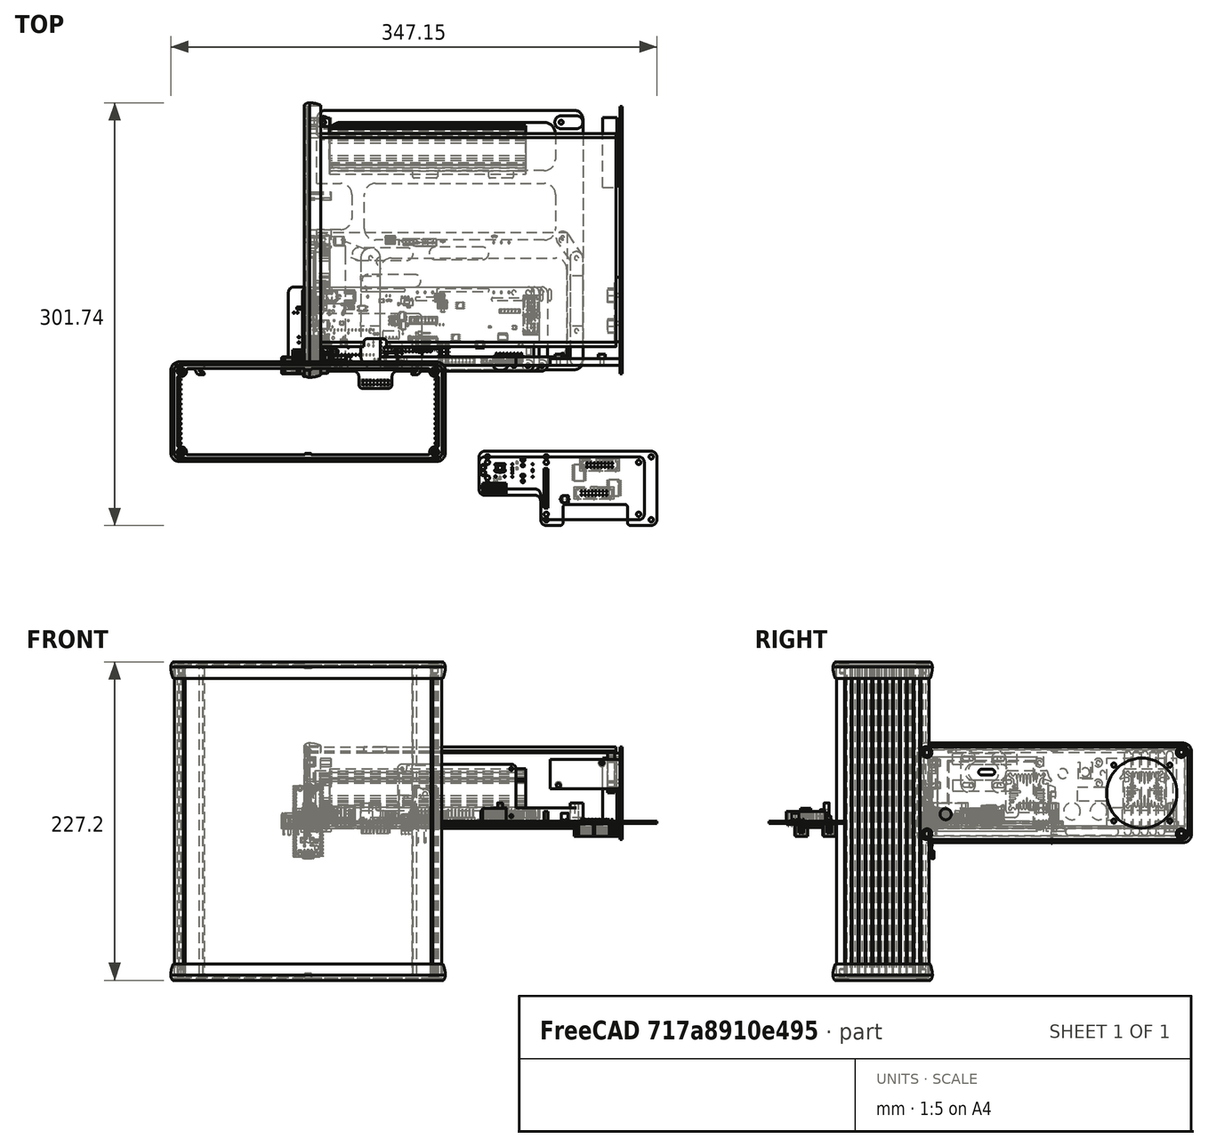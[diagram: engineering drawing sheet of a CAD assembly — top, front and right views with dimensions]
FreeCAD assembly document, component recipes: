
FREECAD ASSEMBLY — COMPONENT RECIPES ("EL-Load-CaseV4")

This assembly document has 17 components, labeled P0..P16 below (a component is one placed body or linked part). 7 of them carry a construction recipe — the FreeCAD feature program that regenerates the part from scratch, quoted from this document or its linked companion documents; the rest are supplied as boundary geometry only. No exploded tour is included for this assembly.
COMPONENT P0 — geometry summary ("EL-Load-Analog"; no construction recipe available for this part):
  bounding box: 188.2 x 95.0 x 51.8 mm
  tessellated surface: 174,292 triangles
  volume: 45099 mm^3 (5% of its bounding box)
COMPONENT P1 — geometry summary ("EL-Load-Analog001"; no construction recipe available for this part):
  bounding box: 185.0 x 95.0 x 41.1 mm
  tessellated surface: 106,424 triangles
  volume: 35915 mm^3 (5% of its bounding box)
COMPONENT P2 — geometry summary ("EL-Load-PowerTest2"; no construction recipe available for this part):
  bounding box: 169.3 x 72.5 x 20.0 mm
  tessellated surface: 158,708 triangles
  volume: 24229 mm^3 (10% of its bounding box)
COMPONENT P3 — geometry summary ("EL-Load-PowerTest004"; no construction recipe available for this part):
  bounding box: 175.0 x 72.5 x 20.0 mm
  tessellated surface: 159,700 triangles
  volume: 25175 mm^3 (10% of its bounding box)
COMPONENT P4 — geometry summary ("EL-Load-Panel"; no construction recipe available for this part):
  bounding box: 118.0 x 45.0 x 37.4 mm
  tessellated surface: 35,930 triangles
  volume: 9733 mm^3 (5% of its bounding box)
COMPONENT P5 — geometry summary ("EL-Load-Panel007"; no construction recipe available for this part):
  bounding box: 127.0 x 53.0 x 37.4 mm
  tessellated surface: 55,482 triangles
  volume: 12066 mm^3 (5% of its bounding box)
COMPONENT P6 — geometry summary ("IsolatedPicoprobeV1"; no construction recipe available for this part):
  bounding box: 90.4 x 40.3 x 11.7 mm
  tessellated surface: 22,040 triangles
  volume: 6344 mm^3 (15% of its bounding box)
COMPONENT P7 — geometry summary ("EL-Load-Power-MCU001"; no construction recipe available for this part):
  bounding box: 179.0 x 72.5 x 20.6 mm
  tessellated surface: 201,648 triangles
  volume: 26984 mm^3 (10% of its bounding box)
COMPONENT P8 — recipe-attached ("Heatsink", modeled in this document).
Construction recipe (the document's own serialized feature program — sketch geometry with constraints, then the solid features built on it; lengths are millimeters unless a unit is written):

FEATURE [PartDesign::SubShapeBinder] Binder
  BindCopyOnChange = 0
  BindMode = 0
  ClaimChildren = false
  Context = -> Body [Binder.]
  Fuse = false
  MakeFace = true
  OffsetFill = false
  OffsetIntersection = false
  OffsetJoinType = 0
  OffsetOpenResult = false
  PartialLoad = false
  Relative = true
  Support = -> [Shape125[Face11]]
  _Version = 2
FEATURE [PartDesign::Pad] Pad
  Direction = (1,0,1e-16)
  Length = 140
  Length2 = 10
  Profile = -> Binder
  Suppressed = false
  Type = 0
FEATURE [PartDesign::Body] Body  label="Heatsink"
  AllowCompound = false
  Group = -> [Binder,Pad]
  Origin = -> Origin067
  Tip = -> Pad
COMPONENT P9 — recipe-attached ("PCBFrame1", modeled in this document).
Construction recipe (the document's own serialized feature program — sketch geometry with constraints, then the solid features built on it; lengths are millimeters unless a unit is written):

FEATURE [Sketcher::SketchObject] Sketch
  ArcFitTolerance = 0
  AttachmentSupport = -> [XY_Plane068]
  FullyConstrained = false
  MakeInternals = false
  MapMode = 5
  sketch-geometry (72):
    g0: LineSegment StartX=12.25 StartY=182 StartZ=0 EndX=190.25 EndY=182 EndZ=0
    g1: LineSegment StartX=196.25 StartY=176 StartZ=0 EndX=196.25 EndY=3 EndZ=0
    g2: LineSegment StartX=190.25 StartY=-3 StartZ=0 EndX=12.25 EndY=-3 EndZ=0
    g3: LineSegment StartX=6.25 StartY=3 StartZ=0 EndX=6.25 EndY=97 EndZ=0
    g4: ArcOfCircle CenterX=190.25 CenterY=176 CenterZ=0 NormalX=0 NormalY=0 NormalZ=1 AngleXU=0 Radius=6 StartAngle=-2.7e-15 EndAngle=1.5708
    g5: GeomPoint [constr] X=196.25 Y=182 Z=0
    g6: ArcOfCircle CenterX=190.25 CenterY=3 CenterZ=0 NormalX=0 NormalY=0 NormalZ=1 AngleXU=0 Radius=6 StartAngle=4.71239 EndAngle=6.28319
    g7: GeomPoint [constr] X=196.25 Y=-3 Z=0
    g8: ArcOfCircle CenterX=12.25 CenterY=176 CenterZ=0 NormalX=0 NormalY=0 NormalZ=1 AngleXU=0 Radius=6 StartAngle=1.5708 EndAngle=3.14159
    g9: GeomPoint [constr] X=6.25 Y=182 Z=0
    g10: ArcOfCircle CenterX=12.25 CenterY=3 CenterZ=0 NormalX=0 NormalY=0 NormalZ=1 AngleXU=0 Radius=6 StartAngle=3.14159 EndAngle=4.71239
    g11: GeomPoint [constr] X=6.25 Y=-3 Z=0
    g12: Circle CenterX=11 CenterY=173.498 CenterZ=0 NormalX=0 NormalY=0 NormalZ=1 AngleXU=0 Radius=1.45
    g13: Circle CenterX=11 CenterY=89.4976 CenterZ=0 NormalX=0 NormalY=0 NormalZ=1 AngleXU=0 Radius=1.45
    g14: Circle CenterX=180.742 CenterY=173.605 CenterZ=0 NormalX=0 NormalY=0 NormalZ=1 AngleXU=0 Radius=1.45
    g15: Circle CenterX=181.761 CenterY=91.0561 CenterZ=0 NormalX=0 NormalY=0 NormalZ=1 AngleXU=0 Radius=1.45
    g16: ArcOfCircle CenterX=48.25 CenterY=97.4976 CenterZ=0 NormalX=0 NormalY=0 NormalZ=1 AngleXU=0 Radius=8 StartAngle=3.14159 EndAngle=4.71239
    g17: LineSegment StartX=40.25 StartY=97.4976 StartZ=0 EndX=40.25 EndY=122 EndZ=0
    g18: ArcOfCircle CenterX=48.25 CenterY=122 CenterZ=0 NormalX=0 NormalY=0 NormalZ=1 AngleXU=0 Radius=8 StartAngle=1.5708 EndAngle=3.14159
    g19: LineSegment StartX=48.25 StartY=130 StartZ=0 EndX=168.625 EndY=130 EndZ=0
    g20: ArcOfCircle CenterX=168.625 CenterY=122 CenterZ=0 NormalX=0 NormalY=0 NormalZ=1 AngleXU=0 Radius=8 StartAngle=-9.8e-15 EndAngle=1.5708
    g21: LineSegment StartX=176.625 StartY=122 StartZ=0 EndX=176.625 EndY=97.4976 EndZ=0
    g22: ArcOfCircle CenterX=168.625 CenterY=97.4976 CenterZ=0 NormalX=0 NormalY=0 NormalZ=1 AngleXU=0 Radius=8 StartAngle=4.71239 EndAngle=6.28319
    g23: LineSegment StartX=168.625 StartY=89.4976 StartZ=0 EndX=48.25 EndY=89.4976 EndZ=0
    g24: GeomPoint [constr] X=40.25 Y=89.4976 Z=0
    g25: GeomPoint [constr] X=176.625 Y=130 Z=0
    g26: ArcOfCircle CenterX=23.25 CenterY=147 CenterZ=0 NormalX=0 NormalY=0 NormalZ=1 AngleXU=0 Radius=8 StartAngle=3.14159 EndAngle=4.71239
    g27: LineSegment StartX=15.25 StartY=147 StartZ=0 EndX=15.25 EndY=165.498 EndZ=0
    g28: ArcOfCircle CenterX=23.25 CenterY=165.498 CenterZ=0 NormalX=0 NormalY=0 NormalZ=1 AngleXU=0 Radius=8 StartAngle=1.5708 EndAngle=3.14159
    g29: LineSegment StartX=23.25 StartY=173.498 StartZ=0 EndX=168.564 EndY=173.498 EndZ=0
    g30: ArcOfCircle CenterX=168.564 CenterY=165.498 CenterZ=0 NormalX=0 NormalY=0 NormalZ=1 AngleXU=0 Radius=8 StartAngle=-8e-15 EndAngle=1.5708
    g31: LineSegment StartX=176.564 StartY=165.498 StartZ=0 EndX=176.564 EndY=147 EndZ=0
    g32: ArcOfCircle CenterX=168.564 CenterY=147 CenterZ=0 NormalX=0 NormalY=0 NormalZ=1 AngleXU=0 Radius=8 StartAngle=4.71239 EndAngle=6.28319
    g33: LineSegment StartX=168.564 StartY=139 StartZ=0 EndX=23.25 EndY=139 EndZ=0
    g34: GeomPoint [constr] X=15.25 Y=139 Z=0
    g35: GeomPoint [constr] X=176.564 Y=173.498 Z=0
    g36: LineSegment StartX=6.25 StartY=130 StartZ=0 EndX=23.25 EndY=130 EndZ=0
    g37: ArcOfCircle CenterX=23.25 CenterY=122 CenterZ=0 NormalX=0 NormalY=0 NormalZ=1 AngleXU=0 Radius=8 StartAngle=-9.8e-15 EndAngle=1.5708
    g38: LineSegment StartX=31.25 StartY=122 StartZ=0 EndX=31.25 EndY=105 EndZ=0
    g39: ArcOfCircle CenterX=23.25 CenterY=105 CenterZ=0 NormalX=0 NormalY=0 NormalZ=1 AngleXU=0 Radius=8 StartAngle=4.71239 EndAngle=6.28319
    g40: LineSegment StartX=23.25 StartY=97 StartZ=0 EndX=6.25 EndY=97 EndZ=0
    g41: GeomPoint [constr] X=-2.4437 Y=97 Z=0
    g42: GeomPoint [constr] X=31.25 Y=130 Z=0
    g43: LineSegment StartX=6.25 StartY=130 StartZ=0 EndX=6.25 EndY=176 EndZ=0
    g44: LineSegment [constr] StartX=15.25 StartY=147 StartZ=0 EndX=6.25 EndY=147 EndZ=0
    g45: LineSegment [constr] StartX=11 StartY=173.498 StartZ=0 EndX=16.5518 EndY=169.872 EndZ=0
    g46: LineSegment [constr] StartX=180.742 StartY=173.605 StartZ=0 EndX=175.223 EndY=169.931 EndZ=0
    g47: LineSegment [constr] StartX=181.761 StartY=91.0561 StartZ=0 EndX=175.807 EndY=93.9755 EndZ=0
    g48: LineSegment [constr] StartX=23.25 StartY=130 StartZ=0 EndX=23.25 EndY=139 EndZ=0
    g49: LineSegment [constr] StartX=48.25 StartY=130 StartZ=0 EndX=48.25 EndY=139 EndZ=0
    g50: LineSegment [constr] StartX=31.25 StartY=105 StartZ=0 EndX=40.25 EndY=105 EndZ=0
    g51: Circle CenterX=44.67 CenterY=76.67 CenterZ=0 NormalX=0 NormalY=0 NormalZ=1 AngleXU=0 Radius=1.45
    g52: Circle CenterX=44.67 CenterY=24.67 CenterZ=0 NormalX=0 NormalY=0 NormalZ=1 AngleXU=0 Radius=1.45
    g53: Circle CenterX=191.67 CenterY=24.67 CenterZ=0 NormalX=0 NormalY=0 NormalZ=1 AngleXU=0 Radius=1.45
    g54: Circle CenterX=191.67 CenterY=76.67 CenterZ=0 NormalX=0 NormalY=0 NormalZ=1 AngleXU=0 Radius=1.45
    g55: LineSegment [constr] StartX=44.67 StartY=24.67 StartZ=0 EndX=191.67 EndY=24.67 EndZ=0
    g56: LineSegment [constr] StartX=191.67 StartY=24.67 StartZ=0 EndX=191.67 EndY=76.67 EndZ=0
    g57: LineSegment [constr] StartX=191.67 StartY=76.67 StartZ=0 EndX=44.67 EndY=76.67 EndZ=0
    g58: LineSegment [constr] StartX=44.67 StartY=76.67 StartZ=0 EndX=44.67 EndY=24.67 EndZ=0
    g59: ArcOfCircle CenterX=59.67 CenterY=14 CenterZ=0 NormalX=0 NormalY=0 NormalZ=1 AngleXU=0 Radius=8 StartAngle=3.14159 EndAngle=4.71239
    g60: LineSegment StartX=51.67 StartY=14 StartZ=0 EndX=51.67 EndY=68.67 EndZ=0
    g61: ArcOfCircle CenterX=59.67 CenterY=68.67 CenterZ=0 NormalX=0 NormalY=0 NormalZ=1 AngleXU=0 Radius=8 StartAngle=1.5708 EndAngle=3.14159
    g62: LineSegment StartX=59.67 StartY=76.67 StartZ=0 EndX=176.67 EndY=76.67 EndZ=0
    g63: ArcOfCircle CenterX=176.67 CenterY=68.67 CenterZ=0 NormalX=0 NormalY=0 NormalZ=1 AngleXU=0 Radius=8 StartAngle=-8e-15 EndAngle=1.5708
    g64: LineSegment StartX=184.67 StartY=68.67 StartZ=0 EndX=184.67 EndY=14 EndZ=0
    g65: ArcOfCircle CenterX=176.67 CenterY=14 CenterZ=0 NormalX=0 NormalY=0 NormalZ=1 AngleXU=0 Radius=8 StartAngle=4.71239 EndAngle=6.28319
    g66: LineSegment StartX=176.67 StartY=6 StartZ=0 EndX=59.67 EndY=6 EndZ=0
    g67: GeomPoint [constr] X=51.67 Y=6 Z=0
    g68: GeomPoint [constr] X=184.67 Y=76.67 Z=0
    g69: LineSegment [constr] StartX=59.67 StartY=6 StartZ=0 EndX=59.67 EndY=-3 EndZ=0
    g70: LineSegment [constr] StartX=191.67 StartY=76.67 StartZ=0 EndX=183.729 EndY=72.4347 EndZ=0
    g71: LineSegment [constr] StartX=44.67 StartY=76.67 StartZ=0 EndX=52.6112 EndY=72.4347 EndZ=0
  constraints (180):
    c: Horizontal(g0)
    c: Horizontal(g2)
    c: Vertical(g1)
    c: Vertical(g3)
    c: DistanceY(g11,g9) = 185
    c: DistanceY(g11,g-1) = 3
    c: DistanceX(g-1,g11) = 6.25
    c: DistanceX(g9,g5) = 190
    c: PointOnObject(g5,g0)
    c: PointOnObject(g5,g1)
    c: Tangent(g0,g4) = 1.5708
    c: Tangent(g1,g4) = 1.5708
    c: PointOnObject(g7,g1)
    c: PointOnObject(g7,g2)
    c: Tangent(g1,g6) = 1.5708
    c: Tangent(g2,g6) = 1.5708
    c: PointOnObject(g9,g0)
    c: PointOnObject(g9,g3)
    c: Tangent(g0,g8) = 1.5708
    c: PointOnObject(g11,g2)
    c: PointOnObject(g11,g3)
    c: Tangent(g2,g10) = 1.5708
    c: Tangent(g3,g10) = 1.5708
    c: Equal(g10,g8)
    c: Equal(g8,g4)
    c: Equal(g4,g6)
    c: Radius(g4) = 6
    c: Equal(g15,g14)
    c: Equal(g14,g12)
    c: Equal(g12,g13)
    c: Vertical(g12,g13)
    c: Diameter(g15) = 2.9
    c: DistanceX(g15) = 181.761
    c: DistanceY(g15) = 91.0561
    c: DistanceX(g14) = 180.742
    c: DistanceY(g14) = 173.605
    c: DistanceX(g12) = 11
    c: DistanceY(g12) = 173.498
    c: DistanceY(g13,g12) = 84
    c: Tangent(g16,g17) = 1.5708
    c: Tangent(g17,g18) = 1.5708
    c: Tangent(g18,g19) = 1.5708
    c: Tangent(g19,g20) = 1.5708
    c: Tangent(g20,g21) = 1.5708
    c: Tangent(g21,g22) = 1.5708
    c: Tangent(g22,g23) = 1.5708
    c: Tangent(g23,g16) = 1.5708
    c: Horizontal(g19)
    c: Horizontal(g23)
    c: Vertical(g17)
    c: Vertical(g21)
    c: Equal(g16,g18)
    c: Equal(g18,g20)
    c: Equal(g20,g22)
    c: PointOnObject(g24,g17)
    c: PointOnObject(g24,g23)
    c: PointOnObject(g25,g19)
    c: PointOnObject(g25,g21)
    c: Tangent(g26,g27) = 1.5708
    c: Tangent(g27,g28) = 1.5708
    c: Tangent(g28,g29) = 1.5708
    c: Tangent(g29,g30) = 1.5708
    c: Tangent(g30,g31) = 1.5708
    c: Tangent(g31,g32) = 1.5708
    c: Tangent(g32,g33) = 1.5708
    c: Tangent(g33,g26) = 1.5708
    c: Horizontal(g29)
    c: Horizontal(g33)
    c: Vertical(g27)
    c: Vertical(g31)
    c: Equal(g26,g28)
    c: Equal(g28,g30)
    c: Equal(g30,g32)
    c: PointOnObject(g34,g27)
    c: PointOnObject(g34,g33)
    c: PointOnObject(g35,g29)
    c: PointOnObject(g35,g31)
    c: Tangent(g36,g37) = 1.5708
    c: Tangent(g37,g38) = 1.5708
    c: Tangent(g38,g39) = 1.5708
    c: Tangent(g39,g40) = 1.5708
    c: Horizontal(g36)
    c: Horizontal(g40)
    c: Vertical(g38)
    c: Equal(g37,g39)
    c: PointOnObject(g41,g40)
    c: PointOnObject(g42,g36)
    c: PointOnObject(g42,g38)
    c: Coincident(g3,g40)
    c: Coincident(g43,g36)
    c: Equal(g18,g37)
    c: Equal(g37,g26)
    c: Horizontal(g28,g12)
    c: Coincident(g44,g26)
    c: Horizontal(g44)
    c: Coincident(g45,g12)
    c: PointOnObject(g45,g28)
    c: Perpendicular(g28,g45)
    c: Coincident(g46,g14)
    c: PointOnObject(g46,g30)
    c: Perpendicular(g30,g46)
    c: Equal(g46,g45)
    c: Perpendicular(g22,g47)
    c: Equal(g47,g46)
    c: PointOnObject(g47,g22)
    c: Coincident(g47,g15)
    c: Vertical(g43)
    c: PointOnObject(g44,g43)
    c: Radius(g26) = 8
    c: Vertical(g36,g3)
    c: DistanceY(g36,g0) = 52
    c: DistanceY(g3,g36) = 33
    c: Coincident(g48,g36)
    c: Coincident(g48,g26)
    c: Vertical(g48)
    c: Equal(g48,g44)
    c: Horizontal(g16,g13)
    c: Coincident(g49,g18)
    c: PointOnObject(g49,g33)
    c: Vertical(g49)
    c: Coincident(g50,g38)
    c: PointOnObject(g50,g17)
    c: Horizontal(g50)
    c: Equal(g49,g48)
    c: Equal(g50,g48)
    c: DistanceX(g3,g38) = 25
    c: Tangent(g43,g8) = 1.5708
    c: Equal(g54,g53)
    c: Equal(g53,g52)
    c: Equal(g52,g51)
    c: Equal(g51,g15)
    c: Coincident(g55,g56)
    c: Coincident(g56,g57)
    c: Coincident(g57,g58)
    c: Coincident(g58,g55)
    c: Horizontal(g55)
    c: Horizontal(g57)
    c: Vertical(g56)
    c: Vertical(g58)
    c: Coincident(g52,g55)
    c: Coincident(g54,g56)
    c: Coincident(g55,g53)
    c: Coincident(g57,g51)
    c: DistanceY(g58,g58) = 52
    c: DistanceX(g52,g53) = 147
    c: DistanceX(g52) = 44.67
    c: DistanceY(g52) = 24.67
    c: Tangent(g59,g60) = 1.5708
    c: Tangent(g60,g61) = 1.5708
    c: Tangent(g61,g62) = 1.5708
    c: Tangent(g62,g63) = 1.5708
    c: Tangent(g63,g64) = 1.5708
    c: Tangent(g64,g65) = 1.5708
    c: Tangent(g65,g66) = 1.5708
    c: Tangent(g66,g59) = 1.5708
    c: Horizontal(g62)
    c: Horizontal(g66)
    c: Vertical(g60)
    c: Vertical(g64)
    c: Equal(g59,g61)
    c: Equal(g61,g63)
    c: Equal(g63,g65)
    c: PointOnObject(g67,g60)
    c: PointOnObject(g67,g66)
    c: PointOnObject(g68,g62)
    c: PointOnObject(g68,g64)
    c: Equal(g61,g16)
    c: Horizontal(g61,g51)
    c: Coincident(g69,g59)
    c: PointOnObject(g69,g2)
    c: Vertical(g69)
    c: Equal(g69,g50)
    c: Coincident(g70,g54)
    c: PointOnObject(g70,g63)
    c: Perpendicular(g63,g70)
    c: Coincident(g71,g51)
    c: PointOnObject(g71,g61)
    c: Perpendicular(g61,g71)
    c: Equal(g71,g50)
    c: Equal(g71,g70)
FEATURE [PartDesign::Pad] Pad001
  Direction = (0,0,1)
  Length = 1.6
  Length2 = 10
  Profile = -> Sketch
  ReferenceAxis = -> Sketch [N_Axis]
  Reversed = true
  Suppressed = false
  Type = 0
FEATURE [Sketcher::SketchObject] Sketch001
  ArcFitTolerance = 0
  AttachmentSupport = -> [XY_Plane068]
  ExternalGeometry = -> [Pad001]
  FullyConstrained = true
  MakeInternals = false
  MapMode = 5
  sketch-geometry (12):
    g0: Circle CenterX=191.67 CenterY=76.67 CenterZ=0 NormalX=0 NormalY=0 NormalZ=1 AngleXU=0 Radius=1.45
    g1: Circle CenterX=191.67 CenterY=24.67 CenterZ=0 NormalX=0 NormalY=0 NormalZ=1 AngleXU=0 Radius=1.45
    g2: ArcOfCircle CenterX=44.67 CenterY=76.67 CenterZ=0 NormalX=0 NormalY=0 NormalZ=1 AngleXU=0 Radius=7 StartAngle=9e-16 EndAngle=3.14159
    g3: ArcOfCircle CenterX=44.67 CenterY=7 CenterZ=0 NormalX=0 NormalY=0 NormalZ=1 AngleXU=0 Radius=7 StartAngle=3.14159 EndAngle=6.28319
    g4: LineSegment StartX=37.67 StartY=76.67 StartZ=0 EndX=37.67 EndY=7 EndZ=0
    g5: LineSegment StartX=51.67 StartY=7 StartZ=0 EndX=51.67 EndY=76.67 EndZ=0
    g6: ArcOfCircle CenterX=191.67 CenterY=76.67 CenterZ=0 NormalX=0 NormalY=0 NormalZ=1 AngleXU=0 Radius=4.58 StartAngle=-6.022e-13 EndAngle=3.14159
    g7: ArcOfCircle CenterX=191.67 CenterY=4.58 CenterZ=0 NormalX=0 NormalY=0 NormalZ=1 AngleXU=0 Radius=4.58 StartAngle=3.14159 EndAngle=6.28319
    g8: LineSegment StartX=187.09 StartY=76.67 StartZ=0 EndX=187.09 EndY=4.58 EndZ=0
    g9: LineSegment StartX=196.25 StartY=4.58 StartZ=0 EndX=196.25 EndY=76.67 EndZ=0
    g10: Circle CenterX=44.67 CenterY=76.67 CenterZ=0 NormalX=0 NormalY=0 NormalZ=1 AngleXU=0 Radius=1.45
    g11: Circle CenterX=44.67 CenterY=24.67 CenterZ=0 NormalX=0 NormalY=0 NormalZ=1 AngleXU=0 Radius=1.45
  constraints (24):
    c: Tangent(g3,g5) = -1.5708
    c: Tangent(g4,g3) = -1.5708
    c: Tangent(g4,g2) = -1.5708
    c: Tangent(g5,g2) = -1.5708
    c: Coincident(g10,g2)
    c: Vertical(g4)
    c: Tangent(g8,g6) = -1.5708
    c: Tangent(g6,g9) = -1.5708
    c: Coincident(g0,g6)
    c: Coincident(g-7,g0)
    c: Equal(g-7,g0)
    c: Equal(g1,g-4)
    c: Coincident(g1,g-4)
    c: Tangent(g8,g7) = -1.5708
    c: Tangent(g7,g9) = -1.5708
    c: Vertical(g8)
    c: Tangent(g7,g-5) = 1.5708
    c: Tangent(g3,g-8) = -1.5708
    c: Coincident(g-6,g2)
    c: Equal(g-6,g10)
    c: Coincident(g11,g-9)
    c: Equal(g11,g-9)
    c: Tangent(g-1,g3)
    c: Tangent(g7,g-1)
FEATURE [PartDesign::Pad] Pad002
  BaseFeature = -> Pad001
  Direction = (0,0,1)
  Length = 16.25
  Length2 = 10
  Profile = -> Sketch001
  ReferenceAxis = -> Sketch001 [N_Axis]
  Suppressed = false
  Type = 0
FEATURE [Sketcher::SketchObject] Sketch002
  ArcFitTolerance = 0
  AttachmentSupport = -> [Pad002]
  FullyConstrained = true
  MakeInternals = false
  MapMode = 5
  Placement = pos=(196.25,-1.17838e-10,0) rot=(0.57735,0.57735,0.57735;2.0944rad)
  sketch-geometry (10):
    g0: ArcOfCircle CenterX=31 CenterY=19 CenterZ=0 NormalX=0 NormalY=0 NormalZ=1 AngleXU=0 Radius=3 StartAngle=1.5708 EndAngle=3.14159
    g1: LineSegment StartX=31 StartY=22 StartZ=0 EndX=61 EndY=22 EndZ=0
    g2: ArcOfCircle CenterX=61 CenterY=19 CenterZ=0 NormalX=0 NormalY=0 NormalZ=1 AngleXU=0 Radius=3 StartAngle=-2.71463e-11 EndAngle=1.5708
    g3: LineSegment StartX=64 StartY=19 StartZ=0 EndX=64 EndY=9 EndZ=0
    g4: ArcOfCircle CenterX=61 CenterY=9 CenterZ=0 NormalX=0 NormalY=0 NormalZ=1 AngleXU=0 Radius=3 StartAngle=4.71239 EndAngle=6.28319
    g5: LineSegment StartX=61 StartY=6 StartZ=0 EndX=31 EndY=6 EndZ=0
    g6: ArcOfCircle CenterX=31 CenterY=9 CenterZ=0 NormalX=0 NormalY=0 NormalZ=1 AngleXU=0 Radius=3 StartAngle=3.14159 EndAngle=4.71239
    g7: LineSegment StartX=28 StartY=9 StartZ=0 EndX=28 EndY=19 EndZ=0
    g8: GeomPoint [constr] X=28 Y=22 Z=0
    g9: GeomPoint [constr] X=64 Y=6 Z=0
  constraints (24):
    c: Tangent(g0,g1) = 1.5708
    c: Tangent(g1,g2) = 1.5708
    c: Tangent(g2,g3) = 1.5708
    c: Tangent(g3,g4) = 1.5708
    c: Tangent(g4,g5) = 1.5708
    c: Tangent(g5,g6) = 1.5708
    c: Tangent(g6,g7) = 1.5708
    c: Tangent(g7,g0) = 1.5708
    c: Horizontal(g1)
    c: Horizontal(g5)
    c: Vertical(g3)
    c: Vertical(g7)
    c: Equal(g0,g2)
    c: Equal(g2,g4)
    c: Equal(g4,g6)
    c: PointOnObject(g8,g1)
    c: PointOnObject(g8,g7)
    c: PointOnObject(g9,g3)
    c: PointOnObject(g9,g5)
    c: Radius(g4) = 3
    c: DistanceX(g6,g3) = 36
    c: DistanceY(g-1,g5) = 6
    c: DistanceX(g6) = 28
    c: DistanceY(g3,g2) = 10
FEATURE [PartDesign::Pocket] Pocket
  BaseFeature = -> Pad002
  Direction = (-1,6.004e-13,0)
  Length = 15
  Length2 = 5
  Midplane = true
  Profile = -> Sketch002
  ReferenceAxis = -> Sketch002 [N_Axis]
  Suppressed = false
  Type = 1
FEATURE [Sketcher::SketchObject] Sketch003
  ArcFitTolerance = 0
  AttachmentOffset = pos=(0,0,-0.1) rot=(0,0,1;0rad)
  AttachmentSupport = -> [XY_Plane068]
  ExternalGeometry = -> [Pocket]
  FullyConstrained = true
  MakeInternals = false
  MapMode = 5
  Placement = pos=(0,0,-0.1) rot=(0,0,1;0rad)
  sketch-geometry (22):
    g0: ArcOfCircle CenterX=181.761 CenterY=91.0561 CenterZ=0 NormalX=0 NormalY=0 NormalZ=1 AngleXU=0 Radius=4.58 StartAngle=0.603158 EndAngle=3.74475
    g1: ArcOfCircle CenterX=191.67 CenterY=76.67 CenterZ=0 NormalX=0 NormalY=0 NormalZ=1 AngleXU=0 Radius=4.58 StartAngle=3.74475 EndAngle=6.88634
    g2: LineSegment StartX=177.989 StartY=88.4581 StartZ=0 EndX=187.898 EndY=74.072 EndZ=0
    g3: LineSegment StartX=195.442 StartY=79.268 StartZ=0 EndX=185.533 EndY=93.6541 EndZ=0
    g4: ArcOfCircle CenterX=11 CenterY=89.4976 CenterZ=0 NormalX=0 NormalY=0 NormalZ=1 AngleXU=0 Radius=4.75 StartAngle=1.20679 EndAngle=4.34839
    g5: ArcOfCircle CenterX=44.67 CenterY=76.67 CenterZ=0 NormalX=0 NormalY=0 NormalZ=1 AngleXU=0 Radius=4.75 StartAngle=4.34839 EndAngle=7.48998
    g6: LineSegment StartX=9.30891 StartY=85.0588 StartZ=0 EndX=42.9789 EndY=72.2312 EndZ=0
    g7: LineSegment StartX=46.3611 StartY=81.1088 StartZ=0 EndX=12.6911 EndY=93.9364 EndZ=0
    g8: Circle CenterX=191.67 CenterY=76.67 CenterZ=0 NormalX=0 NormalY=0 NormalZ=1 AngleXU=0 Radius=1.45
    g9: Circle CenterX=181.761 CenterY=91.0561 CenterZ=0 NormalX=0 NormalY=0 NormalZ=1 AngleXU=0 Radius=1.45
    g10: Circle CenterX=44.67 CenterY=76.67 CenterZ=0 NormalX=0 NormalY=0 NormalZ=1 AngleXU=0 Radius=1.45
    g11: Circle CenterX=11 CenterY=89.4976 CenterZ=0 NormalX=0 NormalY=0 NormalZ=1 AngleXU=0 Radius=1.45
    g12: ArcOfCircle CenterX=11 CenterY=173.498 CenterZ=0 NormalX=0 NormalY=0 NormalZ=1 AngleXU=0 Radius=4.25 StartAngle=4.738e-13 EndAngle=3.14159
    g13: ArcOfCircle CenterX=11 CenterY=165.498 CenterZ=0 NormalX=0 NormalY=0 NormalZ=1 AngleXU=0 Radius=4.25 StartAngle=3.14159 EndAngle=6.28319
    g14: LineSegment StartX=6.75 StartY=173.498 StartZ=0 EndX=6.75 EndY=165.498 EndZ=0
    g15: LineSegment StartX=15.25 StartY=165.498 StartZ=0 EndX=15.25 EndY=173.498 EndZ=0
    g16: Circle CenterX=11 CenterY=173.498 CenterZ=0 NormalX=0 NormalY=0 NormalZ=1 AngleXU=0 Radius=1.45
    g17: ArcOfCircle CenterX=180.742 CenterY=173.605 CenterZ=0 NormalX=0 NormalY=0 NormalZ=1 AngleXU=0 Radius=4.58 StartAngle=1.5708 EndAngle=4.71239
    g18: ArcOfCircle CenterX=191.67 CenterY=173.605 CenterZ=0 NormalX=0 NormalY=0 NormalZ=1 AngleXU=0 Radius=4.58 StartAngle=4.71239 EndAngle=7.85398
    g19: LineSegment StartX=180.742 StartY=169.025 StartZ=0 EndX=191.67 EndY=169.025 EndZ=0
    g20: LineSegment StartX=191.67 StartY=178.185 StartZ=0 EndX=180.742 EndY=178.185 EndZ=0
    g21: Circle CenterX=180.742 CenterY=173.605 CenterZ=0 NormalX=0 NormalY=0 NormalZ=1 AngleXU=0 Radius=1.45
  constraints (45):
    c: Tangent(g0,g2) = -1.5708
    c: Tangent(g2,g1) = -1.5708
    c: Tangent(g1,g3) = -1.5708
    c: Tangent(g3,g0) = -1.5708
    c: Equal(g0,g1)
    c: Tangent(g4,g6) = -1.5708
    c: Tangent(g6,g5) = -1.5708
    c: Tangent(g5,g7) = -1.5708
    c: Tangent(g7,g4) = -1.5708
    c: Equal(g4,g5)
    c: Equal(g-5,g8)
    c: Equal(g-3,g9)
    c: Coincident(g10,g5)
    c: Coincident(g11,g4)
    c: Tangent(g12,g14) = -1.5708
    c: Tangent(g14,g13) = -1.5708
    c: Tangent(g13,g15) = -1.5708
    c: Tangent(g15,g12) = -1.5708
    c: Equal(g12,g13)
    c: Coincident(g12,g-8)
    c: Vertical(g14)
    c: Coincident(g16,g12)
    c: Equal(g16,g-8)
    c: Tangent(g17,g19) = -1.5708
    c: Tangent(g19,g18) = -1.5708
    c: Tangent(g18,g20) = -1.5708
    c: Tangent(g20,g17) = -1.5708
    c: Equal(g17,g18)
    c: Coincident(g17,g-4)
    c: Horizontal(g19)
    c: Coincident(g21,g17)
    c: Equal(g21,g-4)
    c: Equal(g0,g17)
    c: Equal(g10,g-9)
    c: Coincident(g5,g-9)
    c: Coincident(g-5,g8)
    c: Coincident(g1,g8)
    c: Equal(g1,g-10)
    c: Tangent(g18,g-11)
    c: Coincident(g-12,g13)
    c: Coincident(g9,g0)
    c: Coincident(g0,g-3)
    c: Equal(g-14,g11)
    c: Coincident(g4,g-14)
    c: Tangent(g4,g-15)
FEATURE [PartDesign::Pad] Pad003
  BaseFeature = -> Pocket
  Direction = (0,0,1)
  Length = 3.4
  Length2 = 10
  Profile = -> Sketch003
  ReferenceAxis = -> Sketch003 [N_Axis]
  Suppressed = false
  Type = 0
FEATURE [Sketcher::SketchObject] Sketch004
  ArcFitTolerance = 0
  AttachmentSupport = -> [XY_Plane068]
  FullyConstrained = true
  MakeInternals = false
  MapMode = 5
  sketch-geometry (20):
    g0: ArcOfCircle CenterX=75.7237 CenterY=139.855 CenterZ=0 NormalX=0 NormalY=0 NormalZ=1 AngleXU=0 Radius=1 StartAngle=1.5708 EndAngle=3.14159
    g1: LineSegment StartX=75.7237 StartY=140.855 StartZ=0 EndX=91.4237 EndY=140.855 EndZ=0
    g2: ArcOfCircle CenterX=91.4237 CenterY=139.855 CenterZ=0 NormalX=0 NormalY=0 NormalZ=1 AngleXU=0 Radius=1 StartAngle=9.8e-15 EndAngle=1.5708
    g3: LineSegment StartX=92.4237 StartY=139.855 StartZ=0 EndX=92.4237 EndY=134.855 EndZ=0
    g4: ArcOfCircle CenterX=91.4237 CenterY=134.855 CenterZ=0 NormalX=0 NormalY=0 NormalZ=1 AngleXU=0 Radius=1 StartAngle=4.71239 EndAngle=6.28319
    g5: LineSegment StartX=91.4237 StartY=133.855 StartZ=0 EndX=75.7237 EndY=133.855 EndZ=0
    g6: ArcOfCircle CenterX=75.7237 CenterY=134.855 CenterZ=0 NormalX=0 NormalY=0 NormalZ=1 AngleXU=0 Radius=1 StartAngle=3.14159 EndAngle=4.71239
    g7: LineSegment StartX=74.7237 StartY=134.855 StartZ=0 EndX=74.7237 EndY=139.855 EndZ=0
    g8: GeomPoint [constr] X=74.7237 Y=140.855 Z=0
    g9: GeomPoint [constr] X=92.4237 Y=133.855 Z=0
    g10: ArcOfCircle CenterX=129.924 CenterY=139.855 CenterZ=0 NormalX=0 NormalY=0 NormalZ=1 AngleXU=0 Radius=1 StartAngle=1.5708 EndAngle=3.14159
    g11: LineSegment StartX=129.924 StartY=140.855 StartZ=0 EndX=145.624 EndY=140.855 EndZ=0
    g12: ArcOfCircle CenterX=145.624 CenterY=139.855 CenterZ=0 NormalX=0 NormalY=0 NormalZ=1 AngleXU=0 Radius=1 StartAngle=-8.9e-15 EndAngle=1.5708
    g13: LineSegment StartX=146.624 StartY=139.855 StartZ=0 EndX=146.624 EndY=134.855 EndZ=0
    g14: ArcOfCircle CenterX=145.624 CenterY=134.855 CenterZ=0 NormalX=0 NormalY=0 NormalZ=1 AngleXU=0 Radius=1 StartAngle=4.71239 EndAngle=6.28319
    g15: LineSegment StartX=145.624 StartY=133.855 StartZ=0 EndX=129.924 EndY=133.855 EndZ=0
    g16: ArcOfCircle CenterX=129.924 CenterY=134.855 CenterZ=0 NormalX=0 NormalY=0 NormalZ=1 AngleXU=0 Radius=1 StartAngle=3.14159 EndAngle=4.71239
    g17: LineSegment StartX=128.924 StartY=134.855 StartZ=0 EndX=128.924 EndY=139.855 EndZ=0
    g18: GeomPoint [constr] X=128.924 Y=140.855 Z=0
    g19: GeomPoint [constr] X=146.624 Y=133.855 Z=0
  constraints (48):
    c: Tangent(g0,g1) = 1.5708
    c: Tangent(g1,g2) = 1.5708
    c: Tangent(g2,g3) = 1.5708
    c: Tangent(g3,g4) = 1.5708
    c: Tangent(g4,g5) = 1.5708
    c: Tangent(g5,g6) = 1.5708
    c: Tangent(g6,g7) = 1.5708
    c: Tangent(g7,g0) = 1.5708
    c: Horizontal(g1)
    c: Horizontal(g5)
    c: Vertical(g3)
    c: Vertical(g7)
    c: Equal(g0,g2)
    c: Equal(g2,g4)
    c: Equal(g4,g6)
    c: PointOnObject(g8,g1)
    c: PointOnObject(g8,g7)
    c: PointOnObject(g9,g3)
    c: PointOnObject(g9,g5)
    c: Tangent(g10,g11) = 1.5708
    c: Tangent(g11,g12) = 1.5708
    c: Tangent(g12,g13) = 1.5708
    c: Tangent(g13,g14) = 1.5708
    c: Tangent(g14,g15) = 1.5708
    c: Tangent(g15,g16) = 1.5708
    c: Tangent(g16,g17) = 1.5708
    c: Tangent(g17,g10) = 1.5708
    c: Horizontal(g11)
    c: Horizontal(g15)
    c: Vertical(g13)
    c: Vertical(g17)
    c: Equal(g10,g12)
    c: Equal(g12,g14)
    c: Equal(g14,g16)
    c: PointOnObject(g18,g11)
    c: PointOnObject(g18,g17)
    c: PointOnObject(g19,g13)
    c: PointOnObject(g19,g15)
    c: Horizontal(g4,g15)
    c: Equal(g1,g11)
    c: Equal(g2,g10)
    c: Horizontal(g10,g1)
    c: DistanceX(g5) = 75.7237
    c: DistanceY(g5) = 133.855
    c: DistanceX(g5,g5) = 15.7
    c: DistanceY(g3,g3) = 5
    c: Radius(g2) = 1
    c: DistanceX(g4,g15) = 38.5
FEATURE [PartDesign::Pocket] Pocket001
  BaseFeature = -> Pad003
  Direction = (0,0,-1)
  Length = 5
  Length2 = 5
  Profile = -> Sketch004
  ReferenceAxis = -> Sketch004 [N_Axis]
  Suppressed = false
  Type = 0
FEATURE [Sketcher::SketchObject] Sketch008
  ArcFitTolerance = 0
  AttachmentSupport = -> [XY_Plane068]
  ExternalGeometry = -> [Pocket001]
  FullyConstrained = true
  MakeInternals = false
  MapMode = 5
  sketch-geometry (6):
    g0: LineSegment StartX=26.73 StartY=3 StartZ=0 EndX=26.73 EndY=85.0588 EndZ=0
    g1: LineSegment StartX=26.73 StartY=85.0588 StartZ=0 EndX=-23.27 EndY=85.0588 EndZ=0
    g2: LineSegment StartX=-23.27 StartY=85.0588 StartZ=0 EndX=-23.27 EndY=-53 EndZ=0
    g3: LineSegment StartX=-23.27 StartY=-53 StartZ=0 EndX=32.73 EndY=-53 EndZ=0
    g4: LineSegment StartX=32.73 StartY=-53 StartZ=0 EndX=32.73 EndY=-3 EndZ=0
    g5: ArcOfCircle CenterX=32.73 CenterY=3 CenterZ=0 NormalX=0 NormalY=0 NormalZ=1 AngleXU=0 Radius=6 StartAngle=3.14159 EndAngle=4.71239
  constraints (18):
    c: Vertical(g0)
    c: Coincident(g1,g0)
    c: Horizontal(g1)
    c: Coincident(g2,g1)
    c: Vertical(g2)
    c: Coincident(g3,g2)
    c: Horizontal(g3)
    c: Coincident(g4,g3)
    c: Vertical(g4)
    c: Equal(g1,g4)
    c: Distance(g4) = 50
    c: Horizontal(g1,g-4)
    c: DistanceX(g0) = 26.73
    c: Coincident(g5,g4)
    c: Perpendicular(g5,g4)
    c: Tangent(g0,g5) = 1.5708
    c: PointOnObject(g4,g-5)
    c: Equal(g-6,g5)
FEATURE [PartDesign::Pocket] Pocket002
  BaseFeature = -> Pocket001
  Direction = (0,0,-1)
  Length = 20
  Length2 = 5
  Midplane = true
  Profile = -> Sketch008
  ReferenceAxis = -> Sketch008 [N_Axis]
  Suppressed = false
  Type = 0
FEATURE [Sketcher::SketchObject] Sketch031
  ArcFitTolerance = 1e-06
  AttachmentOffset = pos=(0,0,-6) rot=(0,0,1;0rad)
  AttachmentSupport = -> [XZ_Plane068]
  ExternalGeometry = -> [Pocket002]
  FullyConstrained = true
  MakeInternals = false
  MapMode = 5
  Placement = pos=(0,6,-1.3e-15) rot=(1,0,0;1.5708rad)
  sketch-geometry (18):
    g0: LineSegment StartX=44.67 StartY=0 StartZ=0 EndX=191.67 EndY=0 EndZ=0
    g1: LineSegment StartX=191.67 StartY=0 StartZ=0 EndX=191.67 EndY=13 EndZ=0
    g2: LineSegment StartX=191.67 StartY=13 StartZ=0 EndX=148.458 EndY=13 EndZ=0
    g3: LineSegment StartX=148.458 StartY=13 StartZ=0 EndX=148.458 EndY=40.7307 EndZ=0
    g4: LineSegment StartX=145.158 StartY=44.0307 StartZ=0 EndX=67.1585 EndY=44.0307 EndZ=0
    g5: LineSegment StartX=63.8585 StartY=40.7307 StartZ=0 EndX=63.8585 EndY=13 EndZ=0
    g6: LineSegment StartX=63.8585 StartY=13 StartZ=0 EndX=44.67 EndY=13 EndZ=0
    g7: LineSegment StartX=44.67 StartY=13 StartZ=0 EndX=44.67 EndY=0 EndZ=0
    g8: Circle CenterX=67.1585 CenterY=40.7307 CenterZ=0 NormalX=0 NormalY=0 NormalZ=1 AngleXU=0 Radius=1.125
    g9: ArcOfCircle CenterX=67.1585 CenterY=40.7307 CenterZ=0 NormalX=0 NormalY=0 NormalZ=1 AngleXU=0 Radius=3.3 StartAngle=1.5708 EndAngle=3.14159
    g10: Circle CenterX=67.1585 CenterY=6.98074 CenterZ=0 NormalX=0 NormalY=0 NormalZ=1 AngleXU=0 Radius=1.125
    g11: ArcOfCircle CenterX=145.158 CenterY=40.7307 CenterZ=0 NormalX=0 NormalY=0 NormalZ=1 AngleXU=0 Radius=3.3 StartAngle=0 EndAngle=1.5708
    g12: Circle CenterX=145.158 CenterY=40.7307 CenterZ=0 NormalX=0 NormalY=0 NormalZ=1 AngleXU=0 Radius=1.125
    g13: Circle CenterX=145.158 CenterY=6.98074 CenterZ=0 NormalX=0 NormalY=0 NormalZ=1 AngleXU=0 Radius=1.125
    g14: LineSegment [constr] StartX=37.67 StartY=8.125 StartZ=0 EndX=44.67 EndY=6e-16 EndZ=0
    g15: LineSegment [constr] StartX=51.67 StartY=8.125 StartZ=0 EndX=44.67 EndY=-3e-16 EndZ=0
    g16: LineSegment [constr] StartX=187.09 StartY=0 StartZ=0 EndX=191.67 EndY=0 EndZ=0
    g17: LineSegment [constr] StartX=196.25 StartY=0 StartZ=0 EndX=191.67 EndY=0 EndZ=0
  constraints (48):
    c: PointOnObject(g0,g-1)
    c: Horizontal(g0)
    c: Coincident(g1,g0)
    c: Vertical(g1)
    c: Coincident(g2,g1)
    c: Horizontal(g2)
    c: Coincident(g3,g2)
    c: Vertical(g3)
    c: Horizontal(g4)
    c: Vertical(g5)
    c: Coincident(g6,g5)
    c: Horizontal(g6)
    c: Coincident(g7,g6)
    c: Vertical(g7)
    c: Coincident(g7,g0)
    c: DistanceX(g5,g3) = 84.6
    c: Diameter(g8) = 2.25
    c: Coincident(g9,g8)
    c: Tangent(g4,g9) = -1.5708
    c: Tangent(g5,g9) = -1.5708
    c: DistanceX(g8) = 67.1585
    c: DistanceY(g8) = 40.7307
    c: Radius(g9) = 3.3
    c: Vertical(g8,g10)
    c: Equal(g10,g8)
    c: Tangent(g4,g11) = -1.5708
    c: Tangent(g3,g11) = -1.5708
    c: Equal(g1,g7)
    c: Coincident(g12,g11)
    c: Equal(g12,g13)
    c: Equal(g13,g8)
    c: Horizontal(g11,g8)
    c: Vertical(g11,g13)
    c: Horizontal(g13,g10)
    c: DistanceY(g10,g8) = 33.75
    c: DistanceY(g1,g1) = 13
    c: Symmetric(g-3,g-3,g14)
    c: Symmetric(g-4,g-4,g15)
    c: Coincident(g15,g14)
    c: Equal(g14,g15)
    c: Coincident(g0,g14)
    c: PointOnObject(g16,g-5)
    c: Horizontal(g16)
    c: PointOnObject(g17,g-6)
    c: Coincident(g17,g16)
    c: Horizontal(g17)
    c: Equal(g16,g17)
    c: Coincident(g16,g0)
FEATURE [PartDesign::Pad] Pad017
  BaseFeature = -> Pocket002
  Direction = (0,-1,2e-16)
  Length = 6
  Length2 = 10
  Profile = -> Sketch031
  ReferenceAxis = -> Sketch031 [N_Axis]
  Suppressed = false
  Type = 0
FEATURE [Sketcher::SketchObject] Sketch032
  ArcFitTolerance = 1e-06
  AttachmentSupport = -> [Pad017]
  ExternalGeometry = -> [Pad017]
  FullyConstrained = true
  MakeInternals = false
  MapMode = 5
  Placement = pos=(0,6,0) rot=(0,0.707107,0.707107;3.14159rad)
  sketch-geometry (7):
    g0: LineSegment StartX=-64.8585 StartY=37.4307 StartZ=0 EndX=-64.8585 EndY=13.0307 EndZ=0
    g1: LineSegment StartX=-95.4585 StartY=13.0307 StartZ=0 EndX=-95.4585 EndY=43.0307 EndZ=0
    g2: LineSegment StartX=-64.8585 StartY=13.0307 StartZ=0 EndX=-95.4585 EndY=13.0307 EndZ=0
    g3: LineSegment StartX=-95.4585 StartY=43.0307 StartZ=0 EndX=-70.4585 EndY=43.0307 EndZ=0
    g4: ArcOfCircle CenterX=-67.1585 CenterY=40.7307 CenterZ=0 NormalX=0 NormalY=0 NormalZ=1 AngleXU=0 Radius=3.3 StartAngle=3.14159 EndAngle=4.71239
    g5: LineSegment StartX=-70.4585 StartY=43.0307 StartZ=0 EndX=-70.4585 EndY=40.7307 EndZ=0
    g6: LineSegment StartX=-67.1585 StartY=37.4307 StartZ=0 EndX=-64.8585 EndY=37.4307 EndZ=0
  constraints (19):
    c: Vertical(g0)
    c: Vertical(g1)
    c: Coincident(g2,g0)
    c: Coincident(g2,g1)
    c: Horizontal(g2)
    c: Coincident(g3,g1)
    c: Horizontal(g3)
    c: DistanceY(g3,g-4) = 1
    c: DistanceX(g0,g-3) = 1
    c: Coincident(g5,g3)
    c: Vertical(g5)
    c: Horizontal(g6)
    c: Coincident(g0,g6)
    c: Coincident(g4,g-5)
    c: Equal(g-6,g4)
    c: DistanceX(g3,g3) = 25
    c: DistanceY(g1,g1) = 30
    c: Tangent(g5,g4) = -1.5708
    c: Tangent(g6,g4) = -1.5708
FEATURE [PartDesign::Pocket] Pocket013
  BaseFeature = -> Pad017
  Direction = (0,-1,2e-16)
  Length = 4
  Length2 = 5
  Profile = -> Sketch032
  ReferenceAxis = -> Sketch032 [N_Axis]
  Suppressed = false
  Type = 0
FEATURE [Sketcher::SketchObject] Sketch033
  ArcFitTolerance = 1e-06
  AttachmentSupport = -> [Pocket013]
  ExternalGeometry = -> [Pocket013]
  FullyConstrained = true
  MakeInternals = false
  MapMode = 5
  Placement = pos=(0,0,16.25) rot=(0,0,1;0rad)
  sketch-geometry (1):
    g0: Circle CenterX=51.67 CenterY=74.25 CenterZ=0 NormalX=0 NormalY=0 NormalZ=1 AngleXU=0 Radius=3
  constraints (3):
    c: Vertical(g0,g-3)
    c: DistanceY(g0) = 74.25
    c: Radius(g0) = 3
FEATURE [PartDesign::Pocket] Pocket014
  BaseFeature = -> Pocket013
  Direction = (0,0,-1)
  Length = 5
  Length2 = 5
  Profile = -> Sketch033
  ReferenceAxis = -> Sketch033 [N_Axis]
  Suppressed = false
  Type = 0
FEATURE [PartDesign::Body] Body001  label="PCBFrame1"
  AllowCompound = false
  Group = -> [Sketch,Pad001,Sketch001,Pad002,Sketch002,Pocket,Sketch003,Pad003,Sketch004,Pocket001,Sketch008,Pocket002,Sketch031,Pad017,Sketch032,Pocket013,Sketch033,Pocket014]
  Origin = -> Origin068
  Placement = pos=(0,0,-3.4) rot=(0,0,1;0rad)
  Tip = -> Pocket014
COMPONENT P10 — recipe-attached ("Front Panel", modeled in this document).
Construction recipe (the document's own serialized feature program — sketch geometry with constraints, then the solid features built on it; lengths are millimeters unless a unit is written):

FEATURE [PartDesign::SubShapeBinder] Binder001
  BindCopyOnChange = 0
  BindMode = 0
  ClaimChildren = false
  Context = -> Body002 [Binder001.]
  Fuse = false
  MakeFace = true
  OffsetFill = false
  OffsetIntersection = false
  OffsetJoinType = 0
  OffsetOpenResult = false
  PartialLoad = false
  Relative = true
  Support = -> [_455U2201[Part__Feature021.]]
  _Version = 2
FEATURE [Sketcher::SketchObject] Sketch006  label="Fan"
  ArcFitTolerance = 0
  AttachmentOffset = pos=(55,-105,0) rot=(0,0,1;0.785398rad)
  AttachmentSupport = -> [YZ_Plane069]
  FullyConstrained = true
  MakeInternals = false
  MapMode = 5
  Placement = pos=(0,55,-105) rot=(0.678598,0.281085,0.678598;2.59356rad)
  sketch-geometry (11):
    g0: LineSegment [constr] StartX=173.5 StartY=33.6 StartZ=0 EndX=141.5 EndY=33.6 EndZ=0
    g1: LineSegment [constr] StartX=141.5 StartY=33.6 StartZ=0 EndX=141.5 EndY=1.6 EndZ=0
    g2: LineSegment [constr] StartX=141.5 StartY=1.6 StartZ=0 EndX=173.5 EndY=1.6 EndZ=0
    g3: LineSegment [constr] StartX=173.5 StartY=1.6 StartZ=0 EndX=173.5 EndY=33.6 EndZ=0
    g4: Circle CenterX=173.5 CenterY=33.6 CenterZ=0 NormalX=0 NormalY=0 NormalZ=1 AngleXU=0 Radius=2
    g5: Circle CenterX=141.5 CenterY=33.6 CenterZ=0 NormalX=0 NormalY=0 NormalZ=1 AngleXU=0 Radius=2
    g6: Circle CenterX=141.5 CenterY=1.6 CenterZ=0 NormalX=0 NormalY=0 NormalZ=1 AngleXU=0 Radius=2
    g7: Circle CenterX=173.5 CenterY=1.6 CenterZ=0 NormalX=0 NormalY=0 NormalZ=1 AngleXU=0 Radius=2
    g8: Circle CenterX=157.5 CenterY=17.6 CenterZ=0 NormalX=0 NormalY=0 NormalZ=1 AngleXU=0 Radius=19.5
    g9: LineSegment [constr] StartX=157.5 StartY=17.6 StartZ=0 EndX=157.5 EndY=33.6 EndZ=0
    g10: LineSegment [constr] StartX=157.5 StartY=17.6 StartZ=0 EndX=157.5 EndY=1.6 EndZ=0
  constraints (28):
    c: Coincident(g0,g1)
    c: Coincident(g1,g2)
    c: Coincident(g2,g3)
    c: Coincident(g3,g0)
    c: Horizontal(g0)
    c: Horizontal(g2)
    c: Vertical(g1)
    c: Vertical(g3)
    c: Equal(g1,g2)
    c: Coincident(g4,g0)
    c: Coincident(g5,g0)
    c: Coincident(g6,g1)
    c: Coincident(g7,g2)
    c: Equal(g7,g6)
    c: Equal(g6,g5)
    c: Equal(g5,g4)
    c: Diameter(g6) = 4
    c: Coincident(g9,g8)
    c: Vertical(g9)
    c: Symmetric(g5,g4,g9)
    c: Diameter(g8) = 39
    c: Coincident(g10,g8)
    c: PointOnObject(g10,g2)
    c: Vertical(g10)
    c: Equal(g10,g9)
    c: Distance(g0) = 32
    c: DistanceX(g7) = 173.5
    c: DistanceY(g7) = 1.6
FEATURE [Sketcher::SketchObject] Sketch007  label="Panel"
  ArcFitTolerance = 0
  AttachmentSupport = -> [YZ_Plane069]
  ExternalGeometry = -> [Binder001]
  FullyConstrained = true
  MakeInternals = false
  MapMode = 5
  Placement = pos=(0,0,0) rot=(0.57735,0.57735,0.57735;2.0944rad)
  sketch-geometry (18):
    g0: ArcOfCircle CenterX=181.1 CenterY=49.2 CenterZ=0 NormalX=0 NormalY=0 NormalZ=1 AngleXU=0 Radius=3.9 StartAngle=-8.429e-13 EndAngle=1.5708
    g1: LineSegment StartX=185 StartY=49.2 StartZ=0 EndX=185 EndY=-9 EndZ=0
    g2: ArcOfCircle CenterX=181.1 CenterY=-9 CenterZ=0 NormalX=0 NormalY=0 NormalZ=1 AngleXU=0 Radius=3.9 StartAngle=4.71239 EndAngle=6.28319
    g3: LineSegment StartX=181.1 StartY=-12.9 StartZ=0 EndX=-2.1 EndY=-12.9 EndZ=0
    g4: ArcOfCircle CenterX=-2.1 CenterY=-9 CenterZ=0 NormalX=0 NormalY=0 NormalZ=1 AngleXU=0 Radius=3.9 StartAngle=3.14159 EndAngle=4.71239
    g5: LineSegment StartX=-6 StartY=-9 StartZ=0 EndX=-6 EndY=49.2 EndZ=0
    g6: ArcOfCircle CenterX=-2.1 CenterY=49.2 CenterZ=0 NormalX=0 NormalY=0 NormalZ=1 AngleXU=0 Radius=3.9 StartAngle=1.5708 EndAngle=3.14159
    g7: LineSegment StartX=-2.1 StartY=53.1 StartZ=0 EndX=181.1 EndY=53.1 EndZ=0
    g8: GeomPoint [constr] X=185 Y=53.1 Z=0
    g9: GeomPoint [constr] X=-6 Y=-12.9 Z=0
    g10: Circle CenterX=180.25 CenterY=49.11 CenterZ=0 NormalX=0 NormalY=0 NormalZ=1 AngleXU=0 Radius=2.1
    g11: Circle CenterX=180.25 CenterY=-8.91 CenterZ=0 NormalX=0 NormalY=0 NormalZ=1 AngleXU=0 Radius=2.1
    g12: Circle CenterX=-1.25 CenterY=-8.91 CenterZ=0 NormalX=0 NormalY=0 NormalZ=1 AngleXU=0 Radius=2.1
    g13: Circle CenterX=-1.25 CenterY=49.11 CenterZ=0 NormalX=0 NormalY=0 NormalZ=1 AngleXU=0 Radius=2.1
    g14: LineSegment [constr] StartX=-1.25 StartY=49.11 StartZ=0 EndX=180.25 EndY=49.11 EndZ=0
    g15: LineSegment [constr] StartX=180.25 StartY=49.11 StartZ=0 EndX=180.25 EndY=-8.91 EndZ=0
    g16: LineSegment [constr] StartX=180.25 StartY=-8.91 StartZ=0 EndX=-1.25 EndY=-8.91 EndZ=0
    g17: LineSegment [constr] StartX=-1.25 StartY=-8.91 StartZ=0 EndX=-1.25 EndY=49.11 EndZ=0
  constraints (42):
    c: Tangent(g0,g1) = 1.5708
    c: Tangent(g1,g2) = 1.5708
    c: Tangent(g2,g3) = 1.5708
    c: Tangent(g3,g4) = 1.5708
    c: Tangent(g4,g5) = 1.5708
    c: Tangent(g5,g6) = 1.5708
    c: Tangent(g6,g7) = 1.5708
    c: Tangent(g7,g0) = 1.5708
    c: Horizontal(g3)
    c: Horizontal(g7)
    c: Vertical(g1)
    c: Vertical(g5)
    c: Equal(g0,g2)
    c: Equal(g2,g4)
    c: Equal(g4,g6)
    c: PointOnObject(g8,g1)
    c: PointOnObject(g8,g7)
    c: PointOnObject(g9,g3)
    c: PointOnObject(g9,g5)
    c: Coincident(g4,g-6)
    c: Coincident(g0,g-4)
    c: PointOnObject(g2,g-5)
    c: Coincident(g14,g15)
    c: Coincident(g15,g16)
    c: Coincident(g16,g17)
    c: Coincident(g17,g14)
    c: Horizontal(g14)
    c: Horizontal(g16)
    c: Vertical(g15)
    c: Vertical(g17)
    c: Coincident(g11,g15)
    c: Coincident(g10,g14)
    c: Coincident(g13,g14)
    c: Coincident(g12,g16)
    c: Equal(g12,g11)
    c: Equal(g11,g10)
    c: Equal(g10,g13)
    c: Diameter(g13) = 4.2
    c: Distance(g17) = 58.02
    c: Distance(g14) = 181.5
    c: DistanceX(g12) = -1.25
    c: DistanceY(g12) = -8.91
FEATURE [Sketcher::SketchObject] Sketch009  label="Fan003"
  ArcFitTolerance = 0
  AttachmentOffset = pos=(3,-6,0) rot=(0,0,1;0rad)
  AttachmentSupport = -> [YZ_Plane069]
  FullyConstrained = true
  MakeInternals = false
  MapMode = 5
  Placement = pos=(0,3,-6) rot=(0.57735,0.57735,0.57735;2.0944rad)
  sketch-geometry (11):
    g0: LineSegment [constr] StartX=173.5 StartY=41.6 StartZ=0 EndX=133.5 EndY=41.6 EndZ=0
    g1: LineSegment [constr] StartX=133.5 StartY=41.6 StartZ=0 EndX=133.5 EndY=1.6 EndZ=0
    g2: LineSegment [constr] StartX=133.5 StartY=1.6 StartZ=0 EndX=173.5 EndY=1.6 EndZ=0
    g3: LineSegment [constr] StartX=173.5 StartY=1.6 StartZ=0 EndX=173.5 EndY=41.6 EndZ=0
    g4: Circle CenterX=173.5 CenterY=41.6 CenterZ=0 NormalX=0 NormalY=0 NormalZ=1 AngleXU=0 Radius=2
    g5: Circle CenterX=133.5 CenterY=41.6 CenterZ=0 NormalX=0 NormalY=0 NormalZ=1 AngleXU=0 Radius=2
    g6: Circle CenterX=133.5 CenterY=1.6 CenterZ=0 NormalX=0 NormalY=0 NormalZ=1 AngleXU=0 Radius=2
    g7: Circle CenterX=173.5 CenterY=1.6 CenterZ=0 NormalX=0 NormalY=0 NormalZ=1 AngleXU=0 Radius=2
    g8: Circle CenterX=153.5 CenterY=21.6 CenterZ=0 NormalX=0 NormalY=0 NormalZ=1 AngleXU=0 Radius=24
    g9: LineSegment [constr] StartX=153.5 StartY=21.6 StartZ=0 EndX=153.5 EndY=41.6 EndZ=0
    g10: LineSegment [constr] StartX=153.5 StartY=21.6 StartZ=0 EndX=153.5 EndY=1.6 EndZ=0
  constraints (28):
    c: Coincident(g0,g1)
    c: Coincident(g1,g2)
    c: Coincident(g2,g3)
    c: Coincident(g3,g0)
    c: Horizontal(g0)
    c: Horizontal(g2)
    c: Vertical(g1)
    c: Vertical(g3)
    c: Equal(g1,g2)
    c: Coincident(g4,g0)
    c: Coincident(g5,g0)
    c: Coincident(g6,g1)
    c: Coincident(g7,g2)
    c: Equal(g7,g6)
    c: Equal(g6,g5)
    c: Equal(g5,g4)
    c: Diameter(g6) = 4
    c: Coincident(g9,g8)
    c: Vertical(g9)
    c: Symmetric(g5,g4,g9)
    c: Diameter(g8) = 48
    c: Coincident(g10,g8)
    c: PointOnObject(g10,g2)
    c: Vertical(g10)
    c: Equal(g10,g9)
    c: Distance(g0) = 40
    c: DistanceX(g7) = 173.5
    c: DistanceY(g7) = 1.6
FEATURE [Sketcher::SketchObject] Sketch010  label="Analog cutouts"
  ArcFitTolerance = 0
  AttachmentSupport = -> [YZ_Plane069]
  FullyConstrained = true
  MakeInternals = false
  MapMode = 5
  Placement = pos=(0,0,0) rot=(0.57735,0.57735,0.57735;2.0944rad)
  sketch-geometry (36):
    g0: Circle CenterX=121.17 CenterY=7 CenterZ=0 NormalX=0 NormalY=0 NormalZ=1 AngleXU=0 Radius=6
    g1: Circle CenterX=102.17 CenterY=7 CenterZ=0 NormalX=0 NormalY=0 NormalZ=1 AngleXU=0 Radius=6
    g2: LineSegment StartX=138.28 StartY=9.5 StartZ=0 EndX=127.88 EndY=9.5 EndZ=0
    g3: LineSegment StartX=127.88 StartY=9.5 StartZ=0 EndX=127.88 EndY=1 EndZ=0
    g4: LineSegment StartX=127.88 StartY=1 StartZ=0 EndX=138.28 EndY=1 EndZ=0
    g5: LineSegment StartX=138.28 StartY=1 StartZ=0 EndX=138.28 EndY=9.5 EndZ=0
    g6: LineSegment [constr] StartX=127.88 StartY=1 StartZ=0 EndX=121.17 EndY=1 EndZ=0
    g7: ArcOfCircle CenterX=172 CenterY=47.45 CenterZ=0 NormalX=0 NormalY=0 NormalZ=1 AngleXU=0 Radius=2.5 StartAngle=5.07e-14 EndAngle=3.14159
    g8: ArcOfCircle CenterX=172 CenterY=-7.55 CenterZ=0 NormalX=0 NormalY=0 NormalZ=1 AngleXU=0 Radius=2.5 StartAngle=3.14159 EndAngle=6.28319
    g9: LineSegment StartX=169.5 StartY=47.45 StartZ=0 EndX=169.5 EndY=-7.55 EndZ=0
    g10: LineSegment StartX=174.5 StartY=-7.55 StartZ=0 EndX=174.5 EndY=47.45 EndZ=0
    g11: ArcOfCircle CenterX=166 CenterY=47.45 CenterZ=0 NormalX=0 NormalY=0 NormalZ=1 AngleXU=0 Radius=2.5 StartAngle=-9.95e-14 EndAngle=3.14159
    g12: ArcOfCircle CenterX=166 CenterY=-7.55 CenterZ=0 NormalX=0 NormalY=0 NormalZ=1 AngleXU=0 Radius=2.5 StartAngle=3.14159 EndAngle=6.28319
    g13: LineSegment StartX=163.5 StartY=47.45 StartZ=0 EndX=163.5 EndY=-7.55 EndZ=0
    g14: LineSegment StartX=168.5 StartY=-7.55 StartZ=0 EndX=168.5 EndY=47.45 EndZ=0
    g15: ArcOfCircle CenterX=160 CenterY=47.45 CenterZ=0 NormalX=0 NormalY=0 NormalZ=1 AngleXU=0 Radius=2.5 StartAngle=-9.33e-14 EndAngle=3.14159
    g16: ArcOfCircle CenterX=160 CenterY=-7.55 CenterZ=0 NormalX=0 NormalY=0 NormalZ=1 AngleXU=0 Radius=2.5 StartAngle=3.14159 EndAngle=6.28319
    g17: LineSegment StartX=157.5 StartY=47.45 StartZ=0 EndX=157.5 EndY=-7.55 EndZ=0
    g18: LineSegment StartX=162.5 StartY=-7.55 StartZ=0 EndX=162.5 EndY=47.45 EndZ=0
    g19: ArcOfCircle CenterX=154 CenterY=47.45 CenterZ=0 NormalX=0 NormalY=0 NormalZ=1 AngleXU=0 Radius=2.5 StartAngle=-7.82e-14 EndAngle=3.14159
    g20: ArcOfCircle CenterX=154 CenterY=-7.55 CenterZ=0 NormalX=0 NormalY=0 NormalZ=1 AngleXU=0 Radius=2.5 StartAngle=3.14159 EndAngle=6.28319
    g21: LineSegment StartX=151.5 StartY=47.45 StartZ=0 EndX=151.5 EndY=-7.55 EndZ=0
    g22: LineSegment StartX=156.5 StartY=-7.55 StartZ=0 EndX=156.5 EndY=47.45 EndZ=0
    g23: ArcOfCircle CenterX=148 CenterY=47.45 CenterZ=0 NormalX=0 NormalY=0 NormalZ=1 AngleXU=0 Radius=2.5 StartAngle=-5.6e-14 EndAngle=3.14159
    g24: ArcOfCircle CenterX=148 CenterY=-7.55 CenterZ=0 NormalX=0 NormalY=0 NormalZ=1 AngleXU=0 Radius=2.5 StartAngle=3.14159 EndAngle=6.28319
    g25: LineSegment StartX=145.5 StartY=47.45 StartZ=0 EndX=145.5 EndY=-7.55 EndZ=0
    g26: LineSegment StartX=150.5 StartY=-7.55 StartZ=0 EndX=150.5 EndY=47.45 EndZ=0
    g27: LineSegment [constr] StartX=169.5 StartY=47.45 StartZ=0 EndX=168.5 EndY=47.45 EndZ=0
    g28: LineSegment [constr] StartX=163.5 StartY=47.45 StartZ=0 EndX=162.5 EndY=47.45 EndZ=0
    g29: LineSegment [constr] StartX=157.5 StartY=47.45 StartZ=0 EndX=156.5 EndY=47.45 EndZ=0
    g30: LineSegment [constr] StartX=151.5 StartY=47.45 StartZ=0 EndX=150.5 EndY=47.45 EndZ=0
    g31: ArcOfCircle CenterX=142 CenterY=47.45 CenterZ=0 NormalX=0 NormalY=0 NormalZ=1 AngleXU=0 Radius=2.5 StartAngle=-3.02e-14 EndAngle=3.14159
    g32: ArcOfCircle CenterX=142 CenterY=-7.55 CenterZ=0 NormalX=0 NormalY=0 NormalZ=1 AngleXU=0 Radius=2.5 StartAngle=3.14159 EndAngle=6.28319
    g33: LineSegment StartX=139.5 StartY=47.45 StartZ=0 EndX=139.5 EndY=-7.55 EndZ=0
    g34: LineSegment StartX=144.5 StartY=-7.55 StartZ=0 EndX=144.5 EndY=47.45 EndZ=0
    g35: LineSegment [constr] StartX=145.5 StartY=47.45 StartZ=0 EndX=144.5 EndY=47.45 EndZ=0
  constraints (90):
    c: Coincident(g2,g3)
    c: Coincident(g3,g4)
    c: Coincident(g4,g5)
    c: Coincident(g5,g2)
    c: Horizontal(g2)
    c: Horizontal(g4)
    c: Vertical(g3)
    c: Vertical(g5)
    c: Horizontal(g0,g1)
    c: Equal(g0,g1)
    c: Diameter(g1) = 12
    c: DistanceX(g2,g2) = 10.4
    c: Distance(g5) = 8.5
    c: DistanceX(g1,g0) = 19
    c: Coincident(g6,g3)
    c: Horizontal(g6)
    c: Tangent(g6,g0) = 1.5708
    c: DistanceY(g-1,g6) = 1
    c: DistanceX(g-1,g1) = 102.17
    c: DistanceX(g6,g6) = 6.71
    c: Tangent(g7,g9) = -1.5708
    c: Tangent(g9,g8) = -1.5708
    c: Tangent(g8,g10) = -1.5708
    c: Tangent(g10,g7) = -1.5708
    c: Equal(g7,g8)
    c: Vertical(g9)
    c: Diameter(g7) = 5
    c: Distance(g10) = 55
    c: DistanceX(g8) = 172
    c: DistanceY(g8) = -7.55
    c: Tangent(g11,g13) = -1.5708
    c: Tangent(g13,g12) = -1.5708
    c: Tangent(g12,g14) = -1.5708
    c: Tangent(g14,g11) = -1.5708
    c: Equal(g11,g12)
    c: Vertical(g13)
    c: Equal(g7,g11)
    c: Equal(g14,g9)
    c: Tangent(g15,g17) = -1.5708
    c: Tangent(g17,g16) = -1.5708
    c: Tangent(g16,g18) = -1.5708
    c: Tangent(g18,g15) = -1.5708
    c: Equal(g15,g16)
    c: Vertical(g17)
    c: Tangent(g19,g21) = -1.5708
    c: Tangent(g21,g20) = -1.5708
    c: Tangent(g20,g22) = -1.5708
    c: Tangent(g22,g19) = -1.5708
    c: Equal(g19,g20)
    c: Vertical(g21)
    c: Equal(g7,g15)
    c: Equal(g7,g19)
    c: Equal(g18,g9)
    c: Equal(g22,g9)
    c: Horizontal(g15,g11)
    c: Horizontal(g11,g7)
    c: Horizontal(g19,g15)
    c: Tangent(g23,g25) = -1.5708
    c: Tangent(g25,g24) = -1.5708
    c: Tangent(g24,g26) = -1.5708
    c: Tangent(g26,g23) = -1.5708
    c: Equal(g23,g24)
    c: Vertical(g25)
    c: Equal(g7,g23)
    c: Equal(g26,g9)
    c: Horizontal(g19,g23)
    c: Coincident(g27,g7)
    c: Coincident(g27,g11)
    c: Coincident(g28,g11)
    c: Coincident(g28,g15)
    c: Coincident(g29,g15)
    c: Coincident(g29,g19)
    c: Coincident(g30,g19)
    c: Coincident(g30,g23)
    c: Equal(g27,g28)
    c: Equal(g28,g29)
    c: Equal(g29,g30)
    c: Distance(g30) = 1
    c: Tangent(g31,g33) = -1.5708
    c: Tangent(g33,g32) = -1.5708
    c: Tangent(g32,g34) = -1.5708
    c: Tangent(g34,g31) = -1.5708
    c: Equal(g31,g32)
    c: Vertical(g33)
    c: Equal(g7,g31)
    c: Equal(g34,g9)
    c: Horizontal(g31,g23)
    c: Coincident(g35,g23)
    c: Coincident(g35,g31)
    c: Equal(g35,g30)
FEATURE [PartDesign::Pad] Pad004
  Direction = (1,0,0)
  Length = 1.83
  Length2 = 10
  Placement = pos=(0,0,0) rot=(1,1,1;2.0944rad)
  Profile = -> Sketch007
  ReferenceAxis = -> Sketch007 [N_Axis]
  Reversed = true
  Suppressed = false
  Type = 0
FEATURE [PartDesign::Chamfer] Chamfer
  Angle = 45
  Base = -> Pad004 [Edge33,Edge36,Edge30,Edge27]
  BaseFeature = -> Pad004
  ChamferType = 0
  FlipDirection = false
  Placement = pos=(0,0,0) rot=(1,1,1;2.0944rad)
  Size = 1.6
  Size2 = 1
  SupportTransform = false
  Suppressed = false
  UseAllEdges = false
FEATURE [PartDesign::Pocket] Pocket003
  BaseFeature = -> Chamfer
  Direction = (-1,0,0)
  Length = 5
  Length2 = 5
  Placement = pos=(0,0,0) rot=(1,1,1;2.0944rad)
  Profile = -> Sketch010
  ReferenceAxis = -> Sketch010 [N_Axis]
  Suppressed = false
  Type = 0
FEATURE [Sketcher::SketchObject] Sketch011
  ArcFitTolerance = 0
  AttachmentSupport = -> [YZ_Plane069]
  FullyConstrained = true
  MakeInternals = false
  MapMode = 5
  Placement = pos=(0,0,0) rot=(0.57735,0.57735,0.57735;2.0944rad)
  sketch-geometry (15):
    g0: Circle CenterX=123.99 CenterY=34.2979 CenterZ=0 NormalX=0 NormalY=0 NormalZ=1 AngleXU=0 Radius=1.75
    g1: Circle CenterX=95.6034 CenterY=33.9737 CenterZ=0 NormalX=0 NormalY=0 NormalZ=1 AngleXU=0 Radius=3.5
    g2: LineSegment StartX=74.79 StartY=42.16 StartZ=0 EndX=14.14 EndY=42.16 EndZ=0
    g3: LineSegment StartX=14.14 StartY=42.16 StartZ=0 EndX=14.14 EndY=-4 EndZ=0
    g4: LineSegment StartX=14.14 StartY=-4 StartZ=0 EndX=74.79 EndY=-4 EndZ=0
    g5: LineSegment StartX=74.79 StartY=-4 StartZ=0 EndX=74.79 EndY=42.16 EndZ=0
    g6: LineSegment StartX=116.776 StartY=42.1588 StartZ=0 EndX=116.776 EndY=30.1588 EndZ=0
    g7: LineSegment StartX=116.776 StartY=30.1588 StartZ=0 EndX=106.776 EndY=30.1588 EndZ=0
    g8: LineSegment StartX=106.776 StartY=30.1588 StartZ=0 EndX=106.776 EndY=42.1588 EndZ=0
    g9: LineSegment StartX=106.776 StartY=42.1588 StartZ=0 EndX=107.776 EndY=42.1588 EndZ=0
    g10: LineSegment StartX=107.776 StartY=42.1588 StartZ=0 EndX=107.776 EndY=31.1588 EndZ=0
    g11: LineSegment StartX=107.776 StartY=31.1588 StartZ=0 EndX=115.776 EndY=31.1588 EndZ=0
    g12: LineSegment StartX=115.776 StartY=31.1588 StartZ=0 EndX=115.776 EndY=42.1588 EndZ=0
    g13: LineSegment StartX=115.776 StartY=42.1588 StartZ=0 EndX=116.776 EndY=42.1588 EndZ=0
    g14: LineSegment [constr] StartX=115.776 StartY=31.1588 StartZ=0 EndX=115.776 EndY=30.1588 EndZ=0
  constraints (45):
    c: Coincident(g2,g3)
    c: Coincident(g3,g4)
    c: Coincident(g4,g5)
    c: Coincident(g5,g2)
    c: Horizontal(g2)
    c: Horizontal(g4)
    c: Vertical(g3)
    c: Vertical(g5)
    c: Vertical(g6)
    c: Coincident(g6,g7)
    c: Horizontal(g7)
    c: Coincident(g7,g8)
    c: Vertical(g8)
    c: Coincident(g8,g9)
    c: Horizontal(g9)
    c: Coincident(g9,g10)
    c: Vertical(g10)
    c: Coincident(g10,g11)
    c: Horizontal(g11)
    c: Coincident(g11,g12)
    c: Vertical(g12)
    c: Coincident(g12,g13)
    c: Coincident(g13,g6)
    c: Horizontal(g13)
    c: Horizontal(g12,g9)
    c: Equal(g13,g9)
    c: Distance(g9) = 1
    c: Coincident(g14,g11)
    c: PointOnObject(g14,g7)
    c: Vertical(g14)
    c: Equal(g14,g13)
    c: Distance(g9,g12) = 8
    c: Distance(g8) = 12
    c: DistanceX(g1) = 95.6034
    c: DistanceY(g1) = 33.9737
    c: DistanceX(g0) = 123.99
    c: DistanceY(g0) = 34.2979
    c: DistanceX(g7) = 106.776
    c: DistanceY(g7) = 30.1588
    c: Diameter(g1) = 7
    c: Diameter(g0) = 3.5
    c: DistanceX(g3) = 14.14
    c: DistanceY(g3) = -4
    c: Distance(g5) = 46.16
    c: Distance(g2) = 60.65
FEATURE [Sketcher::SketchObject] Sketch012
  ArcFitTolerance = 0
  AttachmentSupport = -> [YZ_Plane069]
  FullyConstrained = true
  MakeInternals = false
  MapMode = 5
  Placement = pos=(0,0,0) rot=(0.57735,0.57735,0.57735;2.0944rad)
  sketch-geometry (12):
    g0: Circle CenterX=120.903 CenterY=41.7901 CenterZ=0 NormalX=0 NormalY=0 NormalZ=1 AngleXU=0 Radius=1.45
    g1: Circle CenterX=120.903 CenterY=26.7901 CenterZ=0 NormalX=0 NormalY=0 NormalZ=1 AngleXU=0 Radius=1.45
    g2: Circle CenterX=78.9035 CenterY=41.7901 CenterZ=0 NormalX=0 NormalY=0 NormalZ=1 AngleXU=0 Radius=1.45
    g3: Circle CenterX=3.90349 CenterY=41.7901 CenterZ=0 NormalX=0 NormalY=0 NormalZ=1 AngleXU=0 Radius=1.45
    g4: Circle CenterX=3.90349 CenterY=-3.20994 CenterZ=0 NormalX=0 NormalY=0 NormalZ=1 AngleXU=0 Radius=1.45
    g5: Circle CenterX=78.9035 CenterY=-3.20994 CenterZ=0 NormalX=0 NormalY=0 NormalZ=1 AngleXU=0 Radius=1.45
    g6: Circle CenterX=3.90349 CenterY=-3.20994 CenterZ=0 NormalX=0 NormalY=0 NormalZ=1 AngleXU=0 Radius=3
    g7: Circle CenterX=3.90349 CenterY=41.7901 CenterZ=0 NormalX=0 NormalY=0 NormalZ=1 AngleXU=0 Radius=3
    g8: Circle CenterX=78.9035 CenterY=41.7901 CenterZ=0 NormalX=0 NormalY=0 NormalZ=1 AngleXU=0 Radius=3
    g9: Circle CenterX=120.903 CenterY=41.7901 CenterZ=0 NormalX=0 NormalY=0 NormalZ=1 AngleXU=0 Radius=3
    g10: Circle CenterX=120.903 CenterY=26.7901 CenterZ=0 NormalX=0 NormalY=0 NormalZ=1 AngleXU=0 Radius=3
    g11: Circle CenterX=78.9035 CenterY=-3.20994 CenterZ=0 NormalX=0 NormalY=0 NormalZ=1 AngleXU=0 Radius=3
  constraints (30):
    c: Horizontal(g0,g2)
    c: Horizontal(g2,g3)
    c: Horizontal(g5,g4)
    c: Vertical(g5,g2)
    c: Vertical(g1,g0)
    c: Vertical(g4,g3)
    c: Equal(g4,g3)
    c: Equal(g3,g2)
    c: Equal(g2,g5)
    c: Equal(g5,g1)
    c: Equal(g1,g0)
    c: Distance(g0,g1) = 15
    c: Distance(g0,g2) = 42
    c: DistanceX(g3,g2) = 75
    c: DistanceY(g4,g3) = 45
    c: Diameter(g5) = 2.9
    c: DistanceX(g4) = 3.90349
    c: DistanceY(g4) = -3.20994
    c: Coincident(g6,g4)
    c: Coincident(g7,g3)
    c: Coincident(g8,g2)
    c: Coincident(g9,g0)
    c: Coincident(g10,g1)
    c: Coincident(g11,g5)
    c: Diameter(g11) = 6
    c: Equal(g11,g10)
    c: Equal(g10,g9)
    c: Equal(g9,g8)
    c: Equal(g8,g7)
    c: Equal(g7,g6)
FEATURE [PartDesign::Pad] Pad005
  BaseFeature = -> Pocket003
  Direction = (1,0,0)
  Length = 4.5
  Length2 = 10
  Placement = pos=(0,0,0) rot=(1,1,1;2.0944rad)
  Profile = -> Sketch012
  ReferenceAxis = -> Sketch012 [N_Axis]
  Suppressed = false
  Type = 0
FEATURE [PartDesign::Pocket] Pocket004
  BaseFeature = -> Pad005
  Direction = (-1,0,0)
  Length = 15
  Length2 = 5
  Midplane = true
  Placement = pos=(0,0,0) rot=(1,1,1;2.0944rad)
  Profile = -> Sketch011
  ReferenceAxis = -> Sketch011 [N_Axis]
  Suppressed = false
  Type = 0
FEATURE [PartDesign::Chamfer] Chamfer001
  Angle = 45
  Base = -> Pocket004 [Edge120,Edge117,Edge118,Edge119]
  BaseFeature = -> Pocket004
  ChamferType = 0
  FlipDirection = false
  Placement = pos=(0,0,0) rot=(1,1,1;2.0944rad)
  Size = 1
  Size2 = 1
  SupportTransform = false
  Suppressed = false
  UseAllEdges = false
FEATURE [Sketcher::SketchObject] Sketch013
  ArcFitTolerance = 0
  AttachmentSupport = -> [YZ_Plane069]
  FullyConstrained = true
  MakeInternals = false
  MapMode = 5
  Placement = pos=(0,0,0) rot=(0.57735,0.57735,0.57735;2.0944rad)
  sketch-geometry (4):
    g0: LineSegment StartX=76.75 StartY=45.9 StartZ=0 EndX=6.25 EndY=45.9 EndZ=0
    g1: LineSegment StartX=6.25 StartY=45.9 StartZ=0 EndX=6.25 EndY=-7.1 EndZ=0
    g2: LineSegment StartX=6.25 StartY=-7.1 StartZ=0 EndX=76.75 EndY=-7.1 EndZ=0
    g3: LineSegment StartX=76.75 StartY=-7.1 StartZ=0 EndX=76.75 EndY=45.9 EndZ=0
  constraints (12):
    c: Coincident(g0,g1)
    c: Coincident(g1,g2)
    c: Coincident(g2,g3)
    c: Coincident(g3,g0)
    c: Horizontal(g0)
    c: Horizontal(g2)
    c: Vertical(g1)
    c: Vertical(g3)
    c: DistanceX(g1) = 6.25
    c: DistanceY(g1) = -7.1
    c: DistanceX(g2,g2) = 70.5
    c: DistanceY(g3,g3) = 53
FEATURE [PartDesign::Pocket] Pocket005
  BaseFeature = -> Chamfer001
  Direction = (-1,0,0)
  Length = 5
  Length2 = 5
  Placement = pos=(0,0,0) rot=(1,1,1;2.0944rad)
  Profile = -> Sketch013
  ReferenceAxis = -> Sketch013 [N_Axis]
  Reversed = true
  Suppressed = false
  Type = 0
FEATURE [PartDesign::Pad] Pad006
  BaseFeature = -> Pocket005
  Direction = (1,0,1e-15)
  Length = 0.001
  Length2 = 10
  Placement = pos=(0,0,0) rot=(1,1,1;2.0944rad)
  Profile = -> Pocket005 [Face89]
  Suppressed = false
  Type = 0
FEATURE [PartDesign::Pad] Pad007
  BaseFeature = -> Pad006
  Direction = (4e-16,1,-2e-16)
  Length = 0.001
  Length2 = 10
  Placement = pos=(0,0,0) rot=(1,1,1;2.0944rad)
  Profile = -> Pad006 [Face88]
  Suppressed = false
  Type = 0
FEATURE [Sketcher::SketchObject] Sketch014
  ArcFitTolerance = 0
  AttachmentSupport = -> [YZ_Plane069]
  FullyConstrained = true
  MakeInternals = false
  MapMode = 5
  Placement = pos=(0,0,0) rot=(0.57735,0.57735,0.57735;2.0944rad)
  sketch-geometry (8):
    g0: LineSegment StartX=84 StartY=-5 StartZ=0 EndX=97 EndY=-5 EndZ=0
    g1: LineSegment StartX=97 StartY=-5 StartZ=0 EndX=97 EndY=-7.5 EndZ=0
    g2: LineSegment StartX=97 StartY=-7.5 StartZ=0 EndX=84 EndY=-7.5 EndZ=0
    g3: LineSegment StartX=84 StartY=-7.5 StartZ=0 EndX=84 EndY=-5 EndZ=0
    g4: LineSegment StartX=177 StartY=-5 StartZ=0 EndX=169 EndY=-5 EndZ=0
    g5: LineSegment StartX=169 StartY=-5 StartZ=0 EndX=169 EndY=-7.5 EndZ=0
    g6: LineSegment StartX=169 StartY=-7.5 StartZ=0 EndX=177 EndY=-7.5 EndZ=0
    g7: LineSegment StartX=177 StartY=-7.5 StartZ=0 EndX=177 EndY=-5 EndZ=0
  constraints (24):
    c: Coincident(g0,g1)
    c: Coincident(g1,g2)
    c: Coincident(g2,g3)
    c: Coincident(g3,g0)
    c: Horizontal(g0)
    c: Horizontal(g2)
    c: Vertical(g1)
    c: Vertical(g3)
    c: DistanceY(g3,g3) = 2.5
    c: DistanceX(g2,g2) = 13
    c: Coincident(g4,g5)
    c: Coincident(g5,g6)
    c: Coincident(g6,g7)
    c: Coincident(g7,g4)
    c: Horizontal(g4)
    c: Horizontal(g6)
    c: Vertical(g5)
    c: Vertical(g7)
    c: Horizontal(g0,g4)
    c: Equal(g5,g1)
    c: DistanceX(g4) = 177
    c: DistanceY(g4) = -5
    c: DistanceX(g-1,g0) = 84
    c: DistanceX(g6,g6) = 8
FEATURE [PartDesign::Pad] Pad008
  BaseFeature = -> Pad007
  Direction = (1,0,0)
  Length = 17
  Length2 = 10
  Placement = pos=(0,0,0) rot=(1,1,1;2.0944rad)
  Profile = -> Sketch014
  ReferenceAxis = -> Sketch014 [N_Axis]
  Suppressed = false
  Type = 0
FEATURE [Sketcher::SketchObject] Sketch015
  ArcFitTolerance = 0
  AttachmentSupport = -> [XY_Plane069]
  FullyConstrained = true
  MakeInternals = false
  MapMode = 5
  sketch-geometry (2):
    g0: Circle CenterX=11.8 CenterY=173.5 CenterZ=0 NormalX=0 NormalY=0 NormalZ=1 AngleXU=0 Radius=1.6
    g1: Circle CenterX=11.8 CenterY=89.5 CenterZ=0 NormalX=0 NormalY=0 NormalZ=1 AngleXU=0 Radius=1.6
  constraints (6):
    c: Diameter(g0) = 3.2
    c: DistanceX(g0) = 11.8
    c: DistanceY(g0) = 173.5
    c: Equal(g0,g1)
    c: Vertical(g1,g0)
    c: DistanceY(g1,g0) = 84
FEATURE [PartDesign::Pocket] Pocket006
  BaseFeature = -> Pad008
  Direction = (0,0,-1)
  Length = 32
  Length2 = 5
  Midplane = true
  Placement = pos=(0,0,0) rot=(1,1,1;2.0944rad)
  Profile = -> Sketch015
  ReferenceAxis = -> Sketch015 [N_Axis]
  Suppressed = false
  Type = 0
FEATURE [Sketcher::SketchObject] Sketch016
  ArcFitTolerance = 0
  AttachmentSupport = -> [YZ_Plane069]
  FullyConstrained = true
  MakeInternals = false
  MapMode = 5
  Placement = pos=(0,0,0) rot=(0.57735,0.57735,0.57735;2.0944rad)
  sketch-geometry (4):
    g0: LineSegment StartX=169.017 StartY=10 StartZ=0 EndX=169.017 EndY=-11 EndZ=0
    g1: LineSegment StartX=169.017 StartY=-11 StartZ=0 EndX=175.017 EndY=-11 EndZ=0
    g2: LineSegment StartX=175.017 StartY=-11 StartZ=0 EndX=175.017 EndY=10 EndZ=0
    g3: ArcOfCircle CenterX=172.017 CenterY=10 CenterZ=0 NormalX=0 NormalY=0 NormalZ=1 AngleXU=0 Radius=3 StartAngle=3.14159 EndAngle=6.28319
  constraints (13):
    c: Coincident(g0,g1)
    c: Coincident(g1,g2)
    c: Horizontal(g1)
    c: Vertical(g0)
    c: Vertical(g2)
    c: DistanceX(g0,g2) = 6
    c: DistanceX(g0) = 169.017
    c: DistanceY(g1,g-1) = 11
    c: Coincident(g3,g0)
    c: Coincident(g3,g2)
    c: Horizontal(g2,g3)
    c: Equal(g2,g0)
    c: DistanceY(g2,g2) = 21
FEATURE [PartDesign::Pad] Pad009
  BaseFeature = -> Pocket006
  Direction = (1,0,0)
  Length = 10
  Length2 = 10
  Placement = pos=(0,0,0) rot=(1,1,1;2.0944rad)
  Profile = -> Sketch016
  ReferenceAxis = -> Sketch016 [N_Axis]
  Reversed = true
  Suppressed = false
  Type = 3
  UpToFace = -> Pocket006 [Face1]
FEATURE [Sketcher::SketchObject] Sketch017
  ArcFitTolerance = 0
  AttachmentSupport = -> [YZ_Plane069]
  ExternalGeometry = -> [Pad009]
  FullyConstrained = true
  MakeInternals = false
  MapMode = 5
  Placement = pos=(0,0,0) rot=(0.57735,0.57735,0.57735;2.0944rad)
  sketch-geometry (7):
    g0: ArcOfCircle CenterX=133 CenterY=-7.55 CenterZ=0 NormalX=0 NormalY=0 NormalZ=1 AngleXU=0 Radius=2.5 StartAngle=4.71239 EndAngle=7.85398
    g1: ArcOfCircle CenterX=100 CenterY=-7.55 CenterZ=0 NormalX=0 NormalY=0 NormalZ=1 AngleXU=0 Radius=2.5 StartAngle=1.5708 EndAngle=4.71239
    g2: LineSegment StartX=133 StartY=-5.05 StartZ=0 EndX=100 EndY=-5.05 EndZ=0
    g3: LineSegment StartX=100 StartY=-10.05 StartZ=0 EndX=133 EndY=-10.05 EndZ=0
    g4: Circle CenterX=173.502 CenterY=3.91 CenterZ=0 NormalX=0 NormalY=0 NormalZ=1 AngleXU=0 Radius=1.625
    g5: Circle CenterX=89.5018 CenterY=3.91 CenterZ=0 NormalX=0 NormalY=0 NormalZ=1 AngleXU=0 Radius=1.625
    g6: LineSegment [constr] StartX=133 StartY=-10.05 StartZ=0 EndX=142 EndY=-10.05 EndZ=0
  constraints (18):
    c: Tangent(g0,g2) = -1.5708
    c: Tangent(g2,g1) = -1.5708
    c: Tangent(g1,g3) = -1.5708
    c: Tangent(g3,g0) = -1.5708
    c: Equal(g0,g1)
    c: Horizontal(g2)
    c: Diameter(g0) = 5
    c: DistanceX(g3,g3) = 33
    c: DistanceX(g-1,g1) = 100
    c: Equal(g5,g4)
    c: Horizontal(g4,g5)
    c: DistanceX(g5,g4) = 84
    c: Diameter(g5) = 3.25
    c: DistanceX(g5) = 89.5018
    c: DistanceY(g5) = 3.91
    c: Coincident(g6,g0)
    c: Horizontal(g6)
    c: Tangent(g6,g-3) = -1.5708
FEATURE [PartDesign::Pocket] Pocket007
  BaseFeature = -> Pad009
  Direction = (-1,0,0)
  Length = 5
  Length2 = 5
  Placement = pos=(0,0,0) rot=(1,1,1;2.0944rad)
  Profile = -> Sketch017
  ReferenceAxis = -> Sketch017 [N_Axis]
  Suppressed = false
  Type = 0
FEATURE [Sketcher::SketchObject] Sketch018
  ArcFitTolerance = 0
  AttachmentSupport = -> [YZ_Plane069]
  FullyConstrained = true
  MakeInternals = false
  MapMode = 5
  Placement = pos=(0,0,0) rot=(0.57735,0.57735,0.57735;2.0944rad)
  sketch-geometry (1):
    g0: Circle CenterX=111.65 CenterY=34.9425 CenterZ=0 NormalX=0 NormalY=0 NormalZ=1 AngleXU=0 Radius=3
  constraints (3):
    c: DistanceX(g0) = 111.65
    c: DistanceY(g0) = 34.9425
    c: Diameter(g0) = 6
FEATURE [PartDesign::Pad] Pad010
  BaseFeature = -> Pocket007
  Direction = (1,0,0)
  Length = 1
  Length2 = 10
  Placement = pos=(0,0,0) rot=(1,1,1;2.0944rad)
  Profile = -> Sketch018
  ReferenceAxis = -> Sketch018 [N_Axis]
  Suppressed = false
  Type = 0
FEATURE [Sketcher::SketchObject] Sketch019
  ArcFitTolerance = 0
  AttachmentSupport = -> [YZ_Plane069]
  FullyConstrained = true
  MakeInternals = false
  MapMode = 5
  Placement = pos=(0,0,0) rot=(0.57735,0.57735,0.57735;2.0944rad)
  sketch-geometry (5):
    g0: LineSegment StartX=106 StartY=14.3 StartZ=0 EndX=106 EndY=24.3 EndZ=0
    g1: LineSegment StartX=106 StartY=24.3 StartZ=0 EndX=126 EndY=24.3 EndZ=0
    g2: LineSegment StartX=126 StartY=24.3 StartZ=0 EndX=126 EndY=14.3 EndZ=0
    g3: LineSegment StartX=126 StartY=14.3 StartZ=0 EndX=106 EndY=14.3 EndZ=0
    g4: GeomPoint [constr] X=116 Y=19.3 Z=0
  constraints (13):
    c: Coincident(g0,g1)
    c: Coincident(g1,g2)
    c: Coincident(g2,g3)
    c: Coincident(g3,g0)
    c: Horizontal(g1)
    c: Horizontal(g3)
    c: Vertical(g0)
    c: Vertical(g2)
    c: Symmetric(g1,g0,g4)
    c: DistanceX(g1,g1) = 20
    c: DistanceY(g0,g0) = 10
    c: DistanceX(g4) = 116
    c: DistanceY(g4) = 19.3
FEATURE [PartDesign::Pocket] Pocket008
  BaseFeature = -> Pad010
  Direction = (-1,0,0)
  Length = 5
  Length2 = 5
  Midplane = true
  Placement = pos=(0,0,0) rot=(1,1,1;2.0944rad)
  Profile = -> Sketch019
  ReferenceAxis = -> Sketch019 [N_Axis]
  Suppressed = false
  Type = 1
FEATURE [PartDesign::Pad] Pad011
  BaseFeature = -> Pocket008
  Direction = (1,0,3.7e-15)
  Length = 12.5
  Length2 = 10
  Placement = pos=(0,0,0) rot=(1,1,1;2.0944rad)
  Profile = -> Pocket008 [Face112]
  Suppressed = false
  Type = 0
FEATURE [PartDesign::Pad] Pad012
  BaseFeature = -> Pad011
  Direction = (1,0,4e-15)
  Length = 12.5
  Length2 = 10
  Placement = pos=(0,0,0) rot=(1,1,1;2.0944rad)
  Profile = -> Pad011 [Face77]
  Suppressed = false
  Type = 0
FEATURE [PartDesign::Body] Body002  label="Front Panel"
  AllowCompound = false
  Group = -> [Binder001,Sketch006,Sketch007,Sketch009,Sketch010,Pad004,Chamfer,Pocket003,Sketch011,Sketch012,Pad005,Pocket004,Chamfer001,Sketch013,Pocket005,Pad006,Pad007,Sketch014,Pad008,Sketch015,Pocket006,Sketch016,Pad009,Sketch017,Pocket007,Sketch018,Pad010,Sketch019,Pocket008,Pad011,Pad012]
  Origin = -> Origin069
  Placement = pos=(-0.6,0,0) rot=(0,0,1;0rad)
  Tip = -> Pad012
COMPONENT P11 — recipe-attached ("RearPanel_DCDCholder", modeled in this document).
Construction recipe (the document's own serialized feature program — sketch geometry with constraints, then the solid features built on it; lengths are millimeters unless a unit is written):

FEATURE [PartDesign::SubShapeBinder] Binder002
  BindCopyOnChange = 0
  BindMode = 0
  ClaimChildren = false
  Context = -> Body004 [Binder002.]
  Fuse = false
  MakeFace = true
  OffsetFill = false
  OffsetIntersection = false
  OffsetJoinType = 0
  OffsetOpenResult = false
  PartialLoad = false
  Relative = true
  Support = -> [Part__Feature561[Face11]]
  _Version = 2
FEATURE [Sketcher::SketchObject] Sketch025
  ArcFitTolerance = 1e-06
  AttachmentOffset = pos=(0,2,0) rot=(0,0,1;0rad)
  AttachmentSupport = -> [XZ_Plane123]
  FullyConstrained = true
  MakeInternals = false
  MapMode = 5
  Placement = pos=(0,4e-16,2) rot=(1,0,0;1.5708rad)
  sketch-geometry (8):
    g0: LineSegment StartX=3.55e-14 StartY=42 StartZ=0 EndX=-50 EndY=42 EndZ=0
    g1: LineSegment StartX=-50 StartY=42 StartZ=0 EndX=-50 EndY=21 EndZ=0
    g2: LineSegment StartX=-50 StartY=21 StartZ=0 EndX=3.55e-14 EndY=21 EndZ=0
    g3: LineSegment StartX=3.55e-14 StartY=21 StartZ=0 EndX=3.55e-14 EndY=42 EndZ=0
    g4: Circle CenterX=-13 CenterY=39.5 CenterZ=0 NormalX=0 NormalY=0 NormalZ=1 AngleXU=0 Radius=1.4
    g5: Circle CenterX=-44 CenterY=23.5 CenterZ=0 NormalX=0 NormalY=0 NormalZ=1 AngleXU=0 Radius=1.4
    g6: LineSegment [constr] StartX=-44 StartY=23.5 StartZ=0 EndX=-44 EndY=21 EndZ=0
    g7: LineSegment [constr] StartX=-13 StartY=39.5 StartZ=0 EndX=-13 EndY=42 EndZ=0
  constraints (24):
    c: Coincident(g0,g1)
    c: Coincident(g1,g2)
    c: Coincident(g2,g3)
    c: Coincident(g3,g0)
    c: Horizontal(g0)
    c: Horizontal(g2)
    c: Vertical(g1)
    c: Vertical(g3)
    c: PointOnObject(g0,g-2)
    c: DistanceX(g0,g0) = 50
    c: DistanceY(g1,g1) = 21
    c: DistanceY(g2) = 21
    c: DistanceY(g5,g4) = 16
    c: DistanceX(g5,g4) = 31
    c: Equal(g5,g4)
    c: Diameter(g5) = 2.8
    c: Coincident(g6,g5)
    c: PointOnObject(g6,g2)
    c: Vertical(g6)
    c: Coincident(g7,g4)
    c: PointOnObject(g7,g0)
    c: Vertical(g7)
    c: Equal(g7,g6)
    c: DistanceX(g1,g5) = 6
FEATURE [PartDesign::Pad] Pad014
  Direction = (0,-1,2e-16)
  Length = 5
  Length2 = 10
  Placement = pos=(0,0,0) rot=(1,0,0;1.5708rad)
  Profile = -> Sketch025
  ReferenceAxis = -> Sketch025 [N_Axis]
  Reversed = true
  Suppressed = false
  Type = 0
FEATURE [Sketcher::SketchObject] Sketch026
  ArcFitTolerance = 1e-06
  AttachmentSupport = -> [Pad014]
  ExternalGeometry = -> [Pad014]
  FullyConstrained = true
  MakeInternals = false
  MapMode = 5
  Placement = pos=(0,5,0) rot=(-1,0,0;1.5708rad)
  sketch-geometry (4):
    g0: Circle CenterX=-13 CenterY=-41.5 CenterZ=0 NormalX=0 NormalY=0 NormalZ=1 AngleXU=0 Radius=1.4
    g1: Circle CenterX=-13 CenterY=-41.5 CenterZ=0 NormalX=0 NormalY=0 NormalZ=1 AngleXU=0 Radius=2.5
    g2: Circle CenterX=-44 CenterY=-25.5 CenterZ=0 NormalX=0 NormalY=0 NormalZ=1 AngleXU=0 Radius=1.4
    g3: Circle CenterX=-44 CenterY=-25.5 CenterZ=0 NormalX=0 NormalY=0 NormalZ=1 AngleXU=0 Radius=2.5
  constraints (8):
    c: Coincident(g0,g-3)
    c: Coincident(g1,g0)
    c: Coincident(g2,g-4)
    c: Coincident(g3,g2)
    c: Equal(g2,g-4)
    c: Equal(g0,g-3)
    c: Tangent(g3,g-5)
    c: Tangent(g1,g-6)
FEATURE [PartDesign::Pad] Pad015
  BaseFeature = -> Pad014
  Direction = (0,1,2e-16)
  Length = 3
  Length2 = 10
  Placement = pos=(0,0,0) rot=(1,0,0;1.5708rad)
  Profile = -> Sketch026
  ReferenceAxis = -> Sketch026 [N_Axis]
  Suppressed = false
  Type = 0
FEATURE [PartDesign::Body] Body004  label="RearPanel_DCDCholder"
  AllowCompound = false
  Group = -> [Binder002,Sketch025,Pad014,Sketch026,Pad015]
  Origin = -> Origin123
  Placement = pos=(222.8,0,0) rot=(0,0,1;0rad)
  Tip = -> Pad015
COMPONENT P12 — recipe-attached ("EndPanel_Cutouts", modeled in this document).
Construction recipe (the document's own serialized feature program — sketch geometry with constraints, then the solid features built on it; lengths are millimeters unless a unit is written):

FEATURE [PartDesign::FeatureBase] Clone
  BaseFeature = -> Part__Feature561
  Placement = pos=(222.8,89.4,20) rot=(0.57735,0.57735,0.57735;2.0944rad)
  Suppressed = false
FEATURE [Sketcher::SketchObject] Sketch028
  ArcFitTolerance = 1e-06
  AttachmentOffset = pos=(0,0,222.8) rot=(0,0,1;0rad)
  AttachmentSupport = -> [YZ_Plane124]
  FullyConstrained = true
  MakeInternals = false
  MapMode = 5
  Placement = pos=(222.8,0,0) rot=(0.57735,0.57735,0.57735;2.0944rad)
  sketch-geometry (15):
    g0: Circle CenterX=12 CenterY=5 CenterZ=0 NormalX=0 NormalY=0 NormalZ=1 AngleXU=0 Radius=4
    g1: Circle CenterX=132 CenterY=40 CenterZ=0 NormalX=0 NormalY=0 NormalZ=1 AngleXU=0 Radius=1.5
    g2: Circle CenterX=172 CenterY=40 CenterZ=0 NormalX=0 NormalY=0 NormalZ=1 AngleXU=0 Radius=1.5
    g3: Circle CenterX=132 CenterY=1.94831e-11 CenterZ=0 NormalX=0 NormalY=0 NormalZ=1 AngleXU=0 Radius=1.5
    g4: Circle CenterX=172 CenterY=1.94831e-11 CenterZ=0 NormalX=0 NormalY=0 NormalZ=1 AngleXU=0 Radius=1.5
    g5: LineSegment [constr] StartX=132 StartY=40 StartZ=0 EndX=132 EndY=1.94831e-11 EndZ=0
    g6: LineSegment [constr] StartX=132 StartY=1.94831e-11 StartZ=0 EndX=172 EndY=1.94831e-11 EndZ=0
    g7: LineSegment [constr] StartX=172 StartY=1.94831e-11 StartZ=0 EndX=172 EndY=40 EndZ=0
    g8: LineSegment [constr] StartX=172 StartY=40 StartZ=0 EndX=132 EndY=40 EndZ=0
    g9: GeomPoint [constr] X=152 Y=20 Z=0
    g10: Circle CenterX=152 CenterY=20 CenterZ=0 NormalX=0 NormalY=0 NormalZ=1 AngleXU=0 Radius=25
    g11: ArcOfCircle CenterX=37.5 CenterY=35 CenterZ=0 NormalX=0 NormalY=0 NormalZ=1 AngleXU=0 Radius=2 StartAngle=1.5708 EndAngle=4.71239
    g12: ArcOfCircle CenterX=45 CenterY=35 CenterZ=0 NormalX=0 NormalY=0 NormalZ=1 AngleXU=0 Radius=2 StartAngle=4.71239 EndAngle=7.85398
    g13: LineSegment StartX=37.5 StartY=37 StartZ=0 EndX=45 EndY=37 EndZ=0
    g14: LineSegment StartX=37.5 StartY=33 StartZ=0 EndX=45 EndY=33 EndZ=0
  constraints (36):
    c: DistanceX(g0) = 12
    c: DistanceY(g0) = 5
    c: Diameter(g0) = 8
    c: Coincident(g5,g6)
    c: Coincident(g6,g7)
    c: Coincident(g7,g8)
    c: Coincident(g8,g5)
    c: Vertical(g5)
    c: Vertical(g7)
    c: Horizontal(g6)
    c: Horizontal(g8)
    c: Symmetric(g7,g5,g9)
    c: Equal(g8,g5)
    c: DistanceX(g8,g8) = 40
    c: Equal(g1,g3)
    c: Equal(g3,g4)
    c: Equal(g4,g2)
    c: Coincident(g5,g1)
    c: Coincident(g5,g3)
    c: Coincident(g6,g4)
    c: Coincident(g7,g2)
    c: Diameter(g4) = 3
    c: PointOnObject(g3,g-1)
    c: Diameter(g10) = 50
    c: Coincident(g10,g9)
    c: DistanceX(g9) = 152
    c: Tangent(g11,g13) = 1.5708
    c: Tangent(g11,g14) = -1.5708
    c: Tangent(g12,g13) = 1.5708
    c: Tangent(g12,g14) = -1.5708
    c: Equal(g11,g12)
    c: Horizontal(g14)
    c: Distance(g11,g12) = 7.5
    c: Radius(g11) = 2
    c: DistanceX(g12) = 45
    c: DistanceY(g12) = 35
FEATURE [PartDesign::Pocket] Pocket011
  BaseFeature = -> Clone
  Direction = (-1,0,0)
  Length = 5
  Length2 = 5
  Placement = pos=(222.8,89.4,20) rot=(0.57735,0.57735,0.57735;2.0944rad)
  Profile = -> Sketch028
  ReferenceAxis = -> Sketch028 [N_Axis]
  Reversed = true
  Suppressed = false
  Type = 0
FEATURE [PartDesign::Plane] DatumPlane
  AttachmentSupport = -> [Pocket011]
  Length = 235.491
  MapMode = 2
  Placement = pos=(222.8,89.4,20) rot=(0.57735,0.57735,0.57735;2.0944rad)
  ResizeMode = 0
  Width = 103.591
FEATURE [Sketcher::SketchObject] Sketch034
  ArcFitTolerance = 1e-06
  AttachmentSupport = -> [DatumPlane]
  ExternalGeometry = -> [Sketch028]
  FullyConstrained = true
  MakeInternals = false
  MapMode = 5
  Placement = pos=(222.8,89.4,20) rot=(0.57735,0.57735,0.57735;2.0944rad)
  sketch-geometry (7):
    g0: ArcOfCircle CenterX=-58.15 CenterY=15 CenterZ=0 NormalX=0 NormalY=0 NormalZ=1 AngleXU=0 Radius=5.5 StartAngle=1.5708 EndAngle=4.71239
    g1: ArcOfCircle CenterX=-38.15 CenterY=15 CenterZ=0 NormalX=0 NormalY=0 NormalZ=1 AngleXU=0 Radius=5.5 StartAngle=4.71239 EndAngle=7.85398
    g2: LineSegment StartX=-58.15 StartY=20.5 StartZ=0 EndX=-38.15 EndY=20.5 EndZ=0
    g3: LineSegment StartX=-58.15 StartY=9.5 StartZ=0 EndX=-38.15 EndY=9.5 EndZ=0
    g4: LineSegment [constr] StartX=-58.15 StartY=15 StartZ=0 EndX=-38.15 EndY=15 EndZ=0
    g5: LineSegment [constr] StartX=-58.15 StartY=15 StartZ=0 EndX=-51.9 EndY=17 EndZ=0
    g6: LineSegment [constr] StartX=-44.4 StartY=13 StartZ=0 EndX=-38.15 EndY=15 EndZ=0
  constraints (15):
    c: Tangent(g0,g2) = 1.5708
    c: Tangent(g0,g3) = -1.5708
    c: Tangent(g1,g2) = 1.5708
    c: Tangent(g1,g3) = -1.5708
    c: Equal(g0,g1)
    c: Distance(g0,g1) = 20
    c: Radius(g0) = 5.5
    c: Coincident(g4,g0)
    c: Coincident(g4,g1)
    c: Symmetric(g-3,g-4,g4)
    c: Coincident(g5,g0)
    c: Coincident(g5,g-3)
    c: Coincident(g6,g-4)
    c: Coincident(g6,g1)
    c: Equal(g6,g5)
FEATURE [PartDesign::Pocket] Pocket015
  BaseFeature = -> Pocket011
  Direction = (-1,0,0)
  Length = 1
  Length2 = 5
  Placement = pos=(222.8,89.4,20) rot=(0.57735,0.57735,0.57735;2.0944rad)
  Profile = -> Sketch034
  ReferenceAxis = -> Sketch034 [N_Axis]
  Reversed = true
  Suppressed = false
  Type = 0
FEATURE [Sketcher::SketchObject] Sketch035
  ArcFitTolerance = 1e-06
  AttachmentOffset = pos=(0,0,-17) rot=(0,0,1;0rad)
  AttachmentSupport = -> [XZ_Plane124]
  ExternalGeometry = -> [Pocket015]
  FullyConstrained = true
  MakeInternals = false
  MapMode = 5
  Placement = pos=(0,17,-3.8e-15) rot=(1,0,0;1.5708rad)
  sketch-geometry (8):
    g0: LineSegment StartX=222.8 StartY=29.5 StartZ=0 EndX=222.8 EndY=21.5 EndZ=0
    g1: LineSegment StartX=222.8 StartY=29.5 StartZ=0 EndX=218.8 EndY=29.5 EndZ=0
    g2: LineSegment StartX=218.8 StartY=29.5 StartZ=0 EndX=218.8 EndY=21.5 EndZ=0
    g3: LineSegment StartX=222.8 StartY=21.5 StartZ=0 EndX=218.8 EndY=21.5 EndZ=0
    g4: LineSegment StartX=222.8 StartY=40.5 StartZ=0 EndX=222.8 EndY=48.5 EndZ=0
    g5: LineSegment StartX=222.8 StartY=48.5 StartZ=0 EndX=218.8 EndY=48.5 EndZ=0
    g6: LineSegment StartX=218.8 StartY=48.5 StartZ=0 EndX=218.8 EndY=40.5 EndZ=0
    g7: LineSegment StartX=218.8 StartY=40.5 StartZ=0 EndX=222.8 EndY=40.5 EndZ=0
  constraints (22):
    c: Vertical(g0)
    c: Horizontal(g1)
    c: Coincident(g2,g1)
    c: Vertical(g2)
    c: Coincident(g3,g0)
    c: Coincident(g3,g2)
    c: Horizontal(g3)
    c: Coincident(g1,g0)
    c: Coincident(g4,g5)
    c: Coincident(g5,g6)
    c: Coincident(g6,g7)
    c: Coincident(g7,g4)
    c: Vertical(g4)
    c: Vertical(g6)
    c: Horizontal(g5)
    c: Horizontal(g7)
    c: Vertical(g1,g6)
    c: Coincident(g4,g-4)
    c: Coincident(g0,g-3)
    c: DistanceX(g5,g5) = 4
    c: DistanceY(g6,g6) = 8
    c: Equal(g6,g2)
FEATURE [PartDesign::Pad] Pad018
  BaseFeature = -> Pocket015
  Direction = (0,-1,2e-16)
  Length = 46
  Length2 = 10
  Placement = pos=(222.8,89.4,20) rot=(0.57735,0.57735,0.57735;2.0944rad)
  Profile = -> Sketch035
  ReferenceAxis = -> Sketch035 [N_Axis]
  Reversed = true
  Suppressed = false
  Type = 0
FEATURE [Sketcher::SketchObject] Sketch036
  ArcFitTolerance = 1e-06
  AttachmentSupport = -> [Pad018]
  ExternalGeometry = -> [Pad018]
  FullyConstrained = true
  MakeInternals = false
  MapMode = 5
  Placement = pos=(218.8,89.4,20) rot=(0.57735,0.57735,-0.57735;4.18879rad)
  sketch-geometry (10):
    g0: Circle CenterX=-39.4 CenterY=-24.5 CenterZ=0 NormalX=0 NormalY=0 NormalZ=1 AngleXU=0 Radius=1.45
    g1: Circle CenterX=-39.4 CenterY=-5.5 CenterZ=0 NormalX=0 NormalY=0 NormalZ=1 AngleXU=0 Radius=1.45
    g2: Circle CenterX=-59.4 CenterY=-5.5 CenterZ=0 NormalX=0 NormalY=0 NormalZ=1 AngleXU=0 Radius=1.45
    g3: Circle CenterX=-59.4 CenterY=-24.5 CenterZ=0 NormalX=0 NormalY=0 NormalZ=1 AngleXU=0 Radius=1.45
    g4: LineSegment [constr] StartX=-59.4 StartY=-5.5 StartZ=0 EndX=-59.4 EndY=-24.5 EndZ=0
    g5: LineSegment [constr] StartX=-59.4 StartY=-24.5 StartZ=0 EndX=-39.4 EndY=-24.5 EndZ=0
    g6: LineSegment [constr] StartX=-39.4 StartY=-24.5 StartZ=0 EndX=-39.4 EndY=-5.5 EndZ=0
    g7: LineSegment [constr] StartX=-39.4 StartY=-5.5 StartZ=0 EndX=-59.4 EndY=-5.5 EndZ=0
    g8: LineSegment [constr] StartX=-72.4 StartY=-1.5 StartZ=0 EndX=-59.4 EndY=-5.5 EndZ=0
    g9: LineSegment [constr] StartX=-39.4 StartY=-5.5 StartZ=0 EndX=-26.4 EndY=-1.5 EndZ=0
  constraints (22):
    c: Diameter(g0) = 2.9
    c: Coincident(g4,g5)
    c: Coincident(g5,g6)
    c: Coincident(g6,g7)
    c: Coincident(g7,g4)
    c: Vertical(g4)
    c: Vertical(g6)
    c: Coincident(g4,g2)
    c: Coincident(g5,g0)
    c: Coincident(g3,g4)
    c: Coincident(g6,g1)
    c: Equal(g0,g3)
    c: Equal(g3,g2)
    c: Equal(g2,g1)
    c: Symmetric(g-3,g-4,g7)
    c: Symmetric(g-5,g-6,g5)
    c: DistanceX(g7,g7) = 20
    c: Coincident(g8,g-4)
    c: Coincident(g9,g1)
    c: Coincident(g9,g-4)
    c: Equal(g8,g9)
    c: Coincident(g8,g2)
FEATURE [PartDesign::Pocket] Pocket016
  BaseFeature = -> Pad018
  Direction = (1,0,0)
  Length = 5
  Length2 = 5
  Placement = pos=(222.8,89.4,20) rot=(0.57735,0.57735,0.57735;2.0944rad)
  Profile = -> Sketch036
  ReferenceAxis = -> Sketch036 [N_Axis]
  Suppressed = false
  Type = 0
FEATURE [PartDesign::Body] Body005  label="EndPanel_Cutouts"
  AllowCompound = false
  Group = -> [Clone,Sketch028,Pocket011,DatumPlane,Sketch034,Pocket015,Sketch035,Pad018,Sketch036,Pocket016]
  Origin = -> Origin124
  Tip = -> Pocket016
COMPONENT P13 — recipe-attached ("Cover", modeled in this document).
Construction recipe (the document's own serialized feature program — sketch geometry with constraints, then the solid features built on it; lengths are millimeters unless a unit is written):

FEATURE [PartDesign::SubShapeBinder] Binder003
  BindCopyOnChange = 0
  BindMode = 0
  ClaimChildren = false
  Context = -> Body006 [Binder003.]
  Fuse = false
  MakeFace = true
  OffsetFill = false
  OffsetIntersection = false
  OffsetJoinType = 0
  OffsetOpenResult = false
  PartialLoad = false
  Relative = true
  Support = -> [Part__Feature562[Face26]]
  _Version = 2
FEATURE [Sketcher::SketchObject] Sketch029
  ArcFitTolerance = 1e-06
  AttachmentSupport = -> [YZ_Plane125]
  ExternalGeometry = -> [Binder003]
  FullyConstrained = true
  MakeInternals = false
  MapMode = 5
  Placement = pos=(0,0,0) rot=(0.57735,0.57735,0.57735;2.0944rad)
  sketch-geometry (8):
    g0: LineSegment StartX=164.88 StartY=48.81 StartZ=0 EndX=14.12 EndY=48.81 EndZ=0
    g1: LineSegment StartX=16.4642 StartY=53.1 StartZ=0 EndX=16.4642 EndY=50.21 EndZ=0
    g2: LineSegment StartX=16.4642 StartY=50.21 StartZ=0 EndX=14.12 EndY=50.21 EndZ=0
    g3: ArcOfCircle CenterX=14.12 CenterY=49.51 CenterZ=0 NormalX=0 NormalY=0 NormalZ=1 AngleXU=0 Radius=0.7 StartAngle=1.5708 EndAngle=4.71239
    g4: LineSegment StartX=16.4642 StartY=53.1 StartZ=0 EndX=162.536 EndY=53.1 EndZ=0
    g5: LineSegment StartX=162.536 StartY=53.1 StartZ=0 EndX=162.536 EndY=50.21 EndZ=0
    g6: LineSegment StartX=162.536 StartY=50.21 StartZ=0 EndX=164.88 EndY=50.21 EndZ=0
    g7: ArcOfCircle CenterX=164.88 CenterY=49.51 CenterZ=0 NormalX=0 NormalY=0 NormalZ=1 AngleXU=0 Radius=0.7 StartAngle=4.71239 EndAngle=7.85398
  constraints (18):
    c: Coincident(g0,g-5)
    c: Coincident(g0,g-4)
    c: Coincident(g1,g-3)
    c: Vertical(g1)
    c: Coincident(g2,g1)
    c: Tangent(g3,g0) = 1.5708
    c: Horizontal(g2)
    c: Tangent(g3,g2) = -1.5708
    c: DistanceY(g0,g2) = 1.4
    c: Coincident(g4,g1)
    c: Coincident(g4,g-3)
    c: Coincident(g5,g4)
    c: Vertical(g5)
    c: Coincident(g6,g5)
    c: Horizontal(g6)
    c: Tangent(g6,g7) = 1.5708
    c: Tangent(g0,g7) = 1.5708
    c: Equal(g7,g3)
FEATURE [PartDesign::Pad] Pad016
  Direction = (1,0,0)
  Length = 220
  Length2 = 10
  Placement = pos=(0,0,0) rot=(1,1,1;2.0944rad)
  Profile = -> Sketch029
  ReferenceAxis = -> Sketch029 [N_Axis]
  Suppressed = false
  Type = 0
FEATURE [Sketcher::SketchObject] Sketch030
  ArcFitTolerance = 1e-06
  AttachmentSupport = -> [XY_Plane125]
  FullyConstrained = true
  MakeInternals = false
  MapMode = 5
  sketch-geometry (10):
    g0: LineSegment StartX=42 StartY=6.104e-13 StartZ=0 EndX=54 EndY=6.104e-13 EndZ=0
    g1: LineSegment StartX=56 StartY=2 StartZ=0 EndX=56 EndY=17 EndZ=0
    g2: LineSegment StartX=54 StartY=19 StartZ=0 EndX=42 EndY=19 EndZ=0
    g3: LineSegment StartX=40 StartY=17 StartZ=0 EndX=40 EndY=2 EndZ=0
    g4: ArcOfCircle CenterX=42 CenterY=2 CenterZ=0 NormalX=0 NormalY=0 NormalZ=1 AngleXU=0 Radius=2 StartAngle=3.14159 EndAngle=4.71239
    g5: ArcOfCircle CenterX=54 CenterY=2 CenterZ=0 NormalX=0 NormalY=0 NormalZ=1 AngleXU=0 Radius=2 StartAngle=4.71239 EndAngle=6.28319
    g6: ArcOfCircle CenterX=54 CenterY=17 CenterZ=0 NormalX=0 NormalY=0 NormalZ=1 AngleXU=0 Radius=2 StartAngle=3.081e-13 EndAngle=1.5708
    g7: ArcOfCircle CenterX=42 CenterY=17 CenterZ=0 NormalX=0 NormalY=0 NormalZ=1 AngleXU=0 Radius=2 StartAngle=1.5708 EndAngle=3.14159
    g8: GeomPoint [constr] X=40 Y=6.776e-13 Z=0
    g9: GeomPoint [constr] X=56 Y=19 Z=0
  constraints (24):
    c: Tangent(g0,g5) = -1.5708
    c: Tangent(g1,g5) = -1.5708
    c: Tangent(g1,g6) = -1.5708
    c: Tangent(g2,g6) = -1.5708
    c: Tangent(g2,g7) = -1.5708
    c: Tangent(g3,g7) = -1.5708
    c: Horizontal(g2)
    c: Vertical(g1)
    c: Vertical(g3)
    c: Equal(g4,g5)
    c: Equal(g5,g6)
    c: Equal(g6,g7)
    c: PointOnObject(g8,g0)
    c: PointOnObject(g8,g3)
    c: PointOnObject(g9,g1)
    c: PointOnObject(g9,g2)
    c: Radius(g5) = 2
    c: Tangent(g4,g0) = -1.5708
    c: Tangent(g4,g3) = -1.5708
    c: PointOnObject(g0,g-1)
    c: Horizontal(g0)
    c: DistanceX(g8) = 40
    c: DistanceX(g3,g1) = 16
    c: DistanceY(g0,g2) = 19
FEATURE [PartDesign::Pocket] Pocket012
  BaseFeature = -> Pad016
  Direction = (0,0,-1)
  Length = 5
  Length2 = 5
  Midplane = true
  Placement = pos=(0,0,0) rot=(1,1,1;2.0944rad)
  Profile = -> Sketch030
  ReferenceAxis = -> Sketch030 [N_Axis]
  Suppressed = false
  Type = 1
FEATURE [PartDesign::Body] Body006  label="Cover"
  AllowCompound = false
  Group = -> [Binder003,Sketch029,Pad016,Sketch030,Pocket012]
  Origin = -> Origin125
  Tip = -> Pocket012
COMPONENT P14 — recipe-attached ("USB clip", modeled in this document).
Construction recipe (the document's own serialized feature program — sketch geometry with constraints, then the solid features built on it; lengths are millimeters unless a unit is written):

FEATURE [PartDesign::SubShapeBinder] Binder004
  BindCopyOnChange = 0
  BindMode = 0
  ClaimChildren = false
  Fuse = false
  MakeFace = true
  OffsetFill = false
  OffsetIntersection = false
  OffsetJoinType = 0
  OffsetOpenResult = false
  PartialLoad = false
  Relative = true
  Support = -> [Body005[Pocket016.Face39]]
  _Version = 2
FEATURE [PartDesign::Plane] DatumPlane001
  AttachmentSupport = -> [Binder004]
  Length = 95.5602
  MapMode = 5
  Placement = pos=(218.8,4.81e-14,0) rot=(0.57735,-0.57735,-0.57735;2.0944rad)
  ResizeMode = 0
  Width = 90.0602
FEATURE [PartDesign::SubShapeBinder] Binder005
  BindCopyOnChange = 0
  BindMode = 0
  ClaimChildren = false
  Context = -> Body007 [Binder005.]
  Fuse = false
  MakeFace = true
  OffsetFill = false
  OffsetIntersection = false
  OffsetJoinType = 0
  OffsetOpenResult = false
  PartialLoad = false
  Relative = true
  Support = -> [Body005[Pocket016.Face38]]
  _Version = 2
FEATURE [Sketcher::SketchObject] Sketch037
  ArcFitTolerance = 1e-06
  AttachmentSupport = -> [DatumPlane001]
  ExternalGeometry = -> [Binder004,Binder005]
  FullyConstrained = true
  MakeInternals = false
  MapMode = 5
  Placement = pos=(218.8,4.81e-14,0) rot=(0.57735,-0.57735,-0.57735;2.0944rad)
  expr: Constraints[33] = .Constraints.dist1
  sketch-geometry (16):
    g0: ArcOfCircle CenterX=-52.5 CenterY=44.5 CenterZ=0 NormalX=0 NormalY=0 NormalZ=1 AngleXU=0 Radius=1.6 StartAngle=1.5708 EndAngle=4.71239
    g1: ArcOfCircle CenterX=-47.5 CenterY=44.5 CenterZ=0 NormalX=0 NormalY=0 NormalZ=1 AngleXU=0 Radius=1.6 StartAngle=4.71239 EndAngle=7.85398
    g2: LineSegment StartX=-52.5 StartY=46.1 StartZ=0 EndX=-47.5 EndY=46.1 EndZ=0
    g3: LineSegment StartX=-52.5 StartY=42.9 StartZ=0 EndX=-47.5 EndY=42.9 EndZ=0
    g4: ArcOfCircle CenterX=-52.5 CenterY=25.5 CenterZ=0 NormalX=0 NormalY=0 NormalZ=1 AngleXU=0 Radius=1.6 StartAngle=1.5708 EndAngle=4.71239
    g5: ArcOfCircle CenterX=-47.5 CenterY=25.5 CenterZ=0 NormalX=0 NormalY=0 NormalZ=1 AngleXU=0 Radius=1.6 StartAngle=4.71239 EndAngle=7.85398
    g6: LineSegment StartX=-52.5 StartY=27.1 StartZ=0 EndX=-47.5 EndY=27.1 EndZ=0
    g7: LineSegment StartX=-52.5 StartY=23.9 StartZ=0 EndX=-47.5 EndY=23.9 EndZ=0
    g8: ArcOfCircle CenterX=-50 CenterY=44.5 CenterZ=0 NormalX=0 NormalY=0 NormalZ=1 AngleXU=0 Radius=5.1 StartAngle=3.54115e-11 EndAngle=3.14159
    g9: ArcOfCircle CenterX=-50 CenterY=25.5 CenterZ=0 NormalX=0 NormalY=0 NormalZ=1 AngleXU=0 Radius=5.1 StartAngle=3.14159 EndAngle=6.28319
    g10: LineSegment StartX=-44.9 StartY=44.5 StartZ=0 EndX=-44.9 EndY=42 EndZ=0
    g11: LineSegment StartX=-55.1 StartY=44.5 StartZ=0 EndX=-55.1 EndY=25.5 EndZ=0
    g12: LineSegment [constr] StartX=-44.9 StartY=44.5 StartZ=0 EndX=-45.9 EndY=44.5 EndZ=0
    g13: ArcOfCircle CenterX=-42.6461 CenterY=35 CenterZ=0 NormalX=0 NormalY=0 NormalZ=1 AngleXU=0 Radius=7.35392 StartAngle=1.8823 EndAngle=4.40088
    g14: LineSegment [constr] StartX=-50 StartY=44.5 StartZ=0 EndX=-50 EndY=25.5 EndZ=0
    g15: LineSegment StartX=-44.9 StartY=28 StartZ=0 EndX=-44.9 EndY=25.5 EndZ=0
  constraints (39):
    c: Tangent(g0,g2) = 1.5708
    c: Tangent(g0,g3) = -1.5708
    c: Tangent(g1,g2) = 1.5708
    c: Tangent(g1,g3) = -1.5708
    c: Equal(g0,g1)
    c: Horizontal(g2)
    c: Symmetric(g0,g1,g-3)
    c: Diameter(g0) = 3.2
    c: Distance(g2) = 5
    c: Tangent(g4,g6) = 1.5708
    c: Tangent(g4,g7) = -1.5708
    c: Tangent(g5,g6) = 1.5708
    c: Tangent(g5,g7) = -1.5708
    c: Equal(g4,g5)
    c: Horizontal(g6)
    c: Symmetric(g5,g4,g-4)
    c: Equal(g4,g0)
    c: Equal(g6,g3)
    c: Tangent(g8,g10) = 1.5708
    c: Tangent(g8,g11) = -1.5708
    c: Tangent(g9,g11) = -1.5708
    c: Equal(g8,g9)
    c: Coincident(g8,g-3)
    c: Coincident(g9,g-4)
    c: Coincident(g12,g8)
    c: PointOnObject(g12,g1)
    c: Horizontal(g12)
    c: DistanceX(g12,g12) = 1
    c: PointOnObject(g13,g15)
    c: Coincident(g14,g8)
    c: Coincident(g14,g9)
    c: Tangent(g14,g13)
    c: DistanceY(g13,g8) = 2.5  'dist1'
    c: DistanceY(g9,g13) = 2.5
    c: Coincident(g10,g13)
    c: PointOnObject(g15,g13)
    c: Vertical(g15)
    c: Tangent(g9,g15) = 1.5708
    c: Vertical(g10)
FEATURE [PartDesign::Pad] Pad019
  Direction = (-1,0,0)
  Length = 5
  Length2 = 10
  Placement = pos=(218.8,0,2.43e-14) rot=(0.57735,-0.57735,-0.57735;2.0944rad)
  Profile = -> Sketch037
  ReferenceAxis = -> Sketch037 [N_Axis]
  Suppressed = false
  Type = 0
FEATURE [PartDesign::Body] Body007  label="USB clip"
  AllowCompound = false
  Group = -> [Binder004,DatumPlane001,Sketch037,Binder005,Pad019]
  Origin = -> Origin145
  Tip = -> Pad019
COMPONENT P15 — geometry summary ("2023_07_19_08_52_50_0648"; no construction recipe available for this part):
  bounding box: 22.9 x 15.7 x 7.8 mm
  tessellated surface: 21,112 triangles
  volume: 1621 mm^3 (58% of its bounding box)
  symmetry: mirror-symmetric across its y mid-plane
COMPONENT P16 — geometry summary ("1455U2201"; no construction recipe available for this part):
  bounding box: 227.2 x 196.1 x 71.1 mm
  tessellated surface: 55,116 triangles
  volume: 243703 mm^3 (8% of its bounding box)
  symmetry: 2-fold rotationally symmetric about the z axis; mirror-symmetric across its x mid-plane, y mid-plane
PROVENANCE & LICENSES
A FreeCAD (.FCStd) document from a public repository crawl; recipes are the document's own serialized feature recipes (and, for linked parts, companion documents' recipes).
License: as declared in the source repository (recorded in the dataset sidecar).
